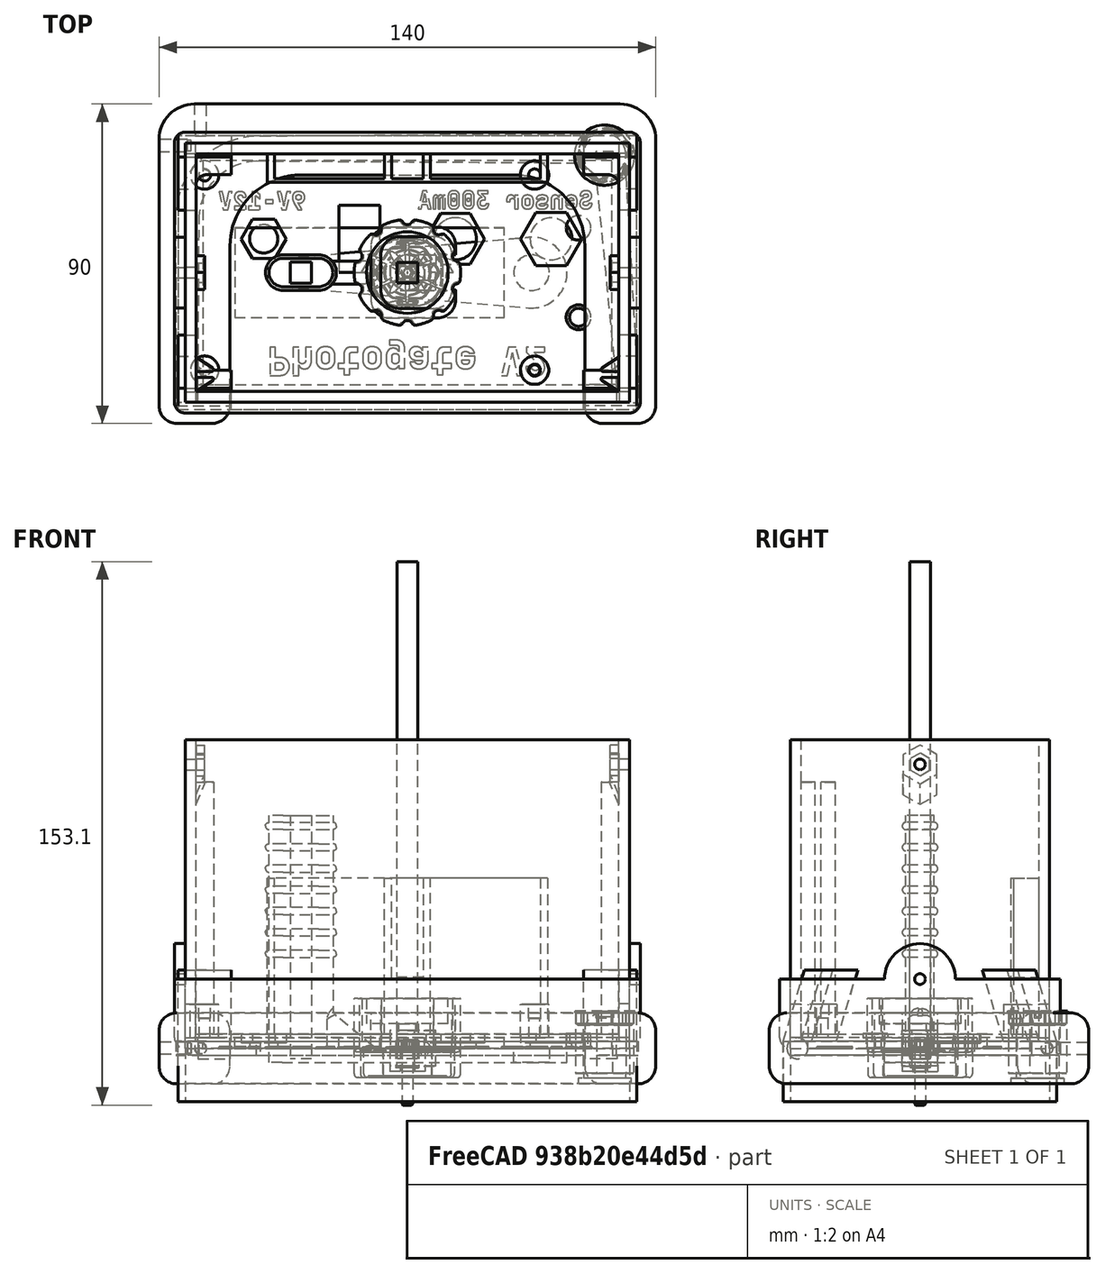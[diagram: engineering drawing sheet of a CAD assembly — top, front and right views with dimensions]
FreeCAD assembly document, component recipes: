
FREECAD ASSEMBLY — COMPONENT RECIPES ("All_Models")

This assembly document has 21 components, labeled P0..P20 below (a component is one placed body or linked part). 17 of them carry a construction recipe — the FreeCAD feature program that regenerates the part from scratch, quoted from this document or its linked companion documents; the rest are supplied as boundary geometry only. No exploded tour is included for this assembly.
NOTE — this tour is split across 2 documents so each fits a 32k-token context. This is document 1: the component sections continue in the remaining 1 document, each repeating the header above.
COMPONENT P0 — recipe-attached ("Arm001", modeled in this document).
Construction recipe (the document's own serialized feature program — sketch geometry with constraints, then the solid features built on it; lengths are millimeters unless a unit is written):

FEATURE [Sketcher::SketchObject] Sketch010
  ArcFitTolerance = 1e-06
  AttachmentSupport = -> [XY_Plane002]
  ExternalTypes = [0]
  FullyConstrained = true
  MakeInternals = false
  MapMode = 5
  _ExternalGeoVersion = 0
  sketch-geometry (9):
    g0: ArcOfCircle CenterX=-35 CenterY=0 CenterZ=0 NormalX=0 NormalY=0 NormalZ=1 AngleXU=0 Radius=4 StartAngle=1.65662 EndAngle=4.62657
    g1: ArcOfCircle CenterX=35 CenterY=0 CenterZ=0 NormalX=0 NormalY=0 NormalZ=1 AngleXU=0 Radius=10 StartAngle=4.62657 EndAngle=7.9398
    g2: LineSegment StartX=-35.3429 StartY=3.98528 StartZ=0 EndX=34.1429 EndY=9.9632 EndZ=0
    g3: LineSegment StartX=-35.3429 StartY=-3.98528 StartZ=0 EndX=34.1429 EndY=-9.9632 EndZ=0
    g4: ArcOfCircle CenterX=-35 CenterY=0 CenterZ=0 NormalX=0 NormalY=0 NormalZ=1 AngleXU=0 Radius=4 StartAngle=1.5708 EndAngle=4.71239
    g5: ArcOfCircle CenterX=-25 CenterY=-1e-16 CenterZ=0 NormalX=0 NormalY=0 NormalZ=1 AngleXU=0 Radius=4 StartAngle=4.71239 EndAngle=7.85398
    g6: LineSegment StartX=-35 StartY=4 StartZ=0 EndX=-25 EndY=4 EndZ=0
    g7: LineSegment StartX=-35 StartY=-4 StartZ=0 EndX=-25 EndY=-4 EndZ=0
    g8: Circle CenterX=35 CenterY=0 CenterZ=0 NormalX=0 NormalY=0 NormalZ=1 AngleXU=0 Radius=5
  constraints (20):
    c: Tangent(g0,g2) = 1.5708
    c: Tangent(g0,g3) = -1.5708
    c: Tangent(g1,g2) = 1.5708
    c: Tangent(g1,g3) = -1.5708
    c: Symmetric(g0,g1,g-1)
    c: DistanceX(g0,g1) = 70
    c: PointOnObject(g0,g-1)
    c: Radius(g0) = 4
    c: Radius(g1) = 10
    c: Tangent(g4,g6) = 1.5708
    c: Tangent(g4,g7) = -1.5708
    c: Tangent(g5,g6) = 1.5708
    c: Tangent(g5,g7) = -1.5708
    c: Equal(g4,g5)
    c: Horizontal(g7)
    c: Coincident(g4,g0)
    c: Tangent(g4,g0)
    c: DistanceX(g0,g5) = 10
    c: Diameter(g8) = 10
    c: Coincident(g8,g1)
FEATURE [PartDesign::Pad] Pad009
  Direction = (0,0,1)
  Length = 4
  Length2 = 10
  Profile = -> Sketch010 [Edge1,Edge2,Edge4,Edge9,Edge3]
  ReferenceAxis = -> Sketch010 [N_Axis]
  Refine = true
  Reversed = true
  SideType = 0
  Suppressed = false
  Type = 0
  Type2 = 0
FEATURE [PartDesign::Pad] Pad010
  BaseFeature = -> Pad009
  Direction = (0,0,1)
  Length = 65.65
  Length2 = 10
  Profile = -> Sketch010 [Edge7,Edge6,Vertex6,Edge5,Edge8]
  ReferenceAxis = -> Sketch010 [N_Axis]
  Refine = true
  SideType = 0
  Suppressed = false
  Type = 0
  Type2 = 0
  expr: Length = Sketch001.Constraints.display_inner_length / 2 + 3 mm
FEATURE [Sketcher::SketchObject] Sketch011
  ArcFitTolerance = 1e-06
  AttachmentOffset = pos=(0,0,-2) rot=(0,0,1;0rad)
  AttachmentSupport = -> [Pad010]
  ExternalTypes = [0]
  FullyConstrained = true
  MakeInternals = false
  MapMode = 5
  Placement = pos=(0,0,63.65) rot=(0,0,1;0rad)
  _ExternalGeoVersion = 0
  sketch-geometry (4):
    g0: ArcOfCircle CenterX=-35 CenterY=0 CenterZ=0 NormalX=0 NormalY=0 NormalZ=1 AngleXU=0 Radius=5 StartAngle=1.5708 EndAngle=4.71239
    g1: ArcOfCircle CenterX=-25 CenterY=-1e-16 CenterZ=0 NormalX=0 NormalY=0 NormalZ=1 AngleXU=0 Radius=5 StartAngle=4.71239 EndAngle=7.85398
    g2: LineSegment StartX=-35 StartY=5 StartZ=0 EndX=-25 EndY=5 EndZ=0
    g3: LineSegment StartX=-35 StartY=-5 StartZ=0 EndX=-25 EndY=-5 EndZ=0
  constraints (8):
    c: Tangent(g0,g2) = 1.5708
    c: Tangent(g0,g3) = -1.5708
    c: Tangent(g1,g2) = 1.5708
    c: Tangent(g1,g3) = -1.5708
    c: Equal(g0,g1)
    c: Radius(g1) = 5
    c: Coincident(g1,g-3)
    c: Coincident(g0,g-4)
FEATURE [PartDesign::Pad] Pad011
  BaseFeature = -> Pad010
  Direction = (0,0,1)
  Length = 2
  Length2 = 10
  Profile = -> Sketch011
  ReferenceAxis = -> Sketch011 [N_Axis]
  Refine = true
  Reversed = true
  SideType = 0
  Suppressed = false
  Type = 0
  Type2 = 0
FEATURE [PartDesign::Fillet] Fillet001
  Base = -> Pad011 [Face14]
  BaseFeature = -> Pad011
  Radius = 0.99
  Refine = true
  SupportTransform = false
  Suppressed = false
  UseAllEdges = false
FEATURE [PartDesign::LinearPattern] LinearPattern
  BaseFeature = -> Fillet001
  Direction = -> Z_Axis002
  Length = 36
  Length2 = 100
  Mode = 1
  Mode2 = 0
  Occurrences = 7
  Occurrences2 = 1
  Offset = 6
  Offset2 = 10
  Originals = -> [Pad011,Fillet001]
  Refine = true
  Reversed = true
  Reversed2 = false
  SpacingPattern = [0]
  SpacingPattern2 = [0]
  Spacings = [-1,-1,-1,-1,-1,-1]
  Suppressed = false
  TransformMode = 0
FEATURE [Sketcher::SketchObject] Sketch057
  ArcFitTolerance = 1e-06
  ExternalTypes = [0]
  FullyConstrained = true
  MakeInternals = false
  MapMode = 5
  _ExternalGeoVersion = 0
  sketch-geometry (5):
    g0: ArcOfCircle CenterX=-25 CenterY=0 CenterZ=0 NormalX=0 NormalY=0 NormalZ=1 AngleXU=0 Radius=3.99999 StartAngle=5.32325 EndAngle=7.24312
    g1: LineSegment StartX=-22.7057 StartY=-3.2766 StartZ=0 EndX=-9.00001 EndY=-3.2766 EndZ=0
    g2: LineSegment StartX=-22.7057 StartY=3.2766 StartZ=0 EndX=-9.00001 EndY=3.2766 EndZ=0
    g3: LineSegment StartX=-9.00001 StartY=3.2766 StartZ=0 EndX=-9.00001 EndY=-3.2766 EndZ=0
    g4: GeomPoint X=-21 Y=0 Z=0
  constraints (14):
    c: Coincident(g0,g-3)
    c: PointOnObject(g0,g-3)
    c: Coincident(g1,g0)
    c: Horizontal(g1)
    c: Coincident(g2,g0)
    c: Horizontal(g2)
    c: Coincident(g3,g2)
    c: Coincident(g3,g1)
    c: Vertical(g3)
    c: Angle(g0) = 1.91986
    c: Vertical(g0,g0)
    c: PointOnObject(g4,g-1)
    c: PointOnObject(g4,g0)
    c: DistanceX(g4,g2) = 12
FEATURE [PartDesign::Pad] Pad033
  BaseFeature = -> LinearPattern
  Direction = (-1.2,0,1)
  Length = 12
  Length2 = 10
  Profile = -> Sketch057
  ReferenceAxis = -> Sketch057 [N_Axis]
  Refine = true
  SideType = 0
  Suppressed = false
  Type = 0
  Type2 = 0
  UseCustomVector = true
FEATURE [PartDesign::Fillet] Fillet006
  Base = -> Pad033 [Face137]
  BaseFeature = -> Pad033
  Radius = 2.5
  Refine = true
  SupportTransform = false
  Suppressed = false
  UseAllEdges = false
FEATURE [Sketcher::SketchObject] Sketch045
  ArcFitTolerance = 1e-06
  AttachmentSupport = -> [Fillet006]
  ExternalTypes = [0]
  FullyConstrained = true
  MakeInternals = false
  MapMode = 5
  Placement = pos=(0,0,65.65) rot=(0,0,1;0rad)
  _ExternalGeoVersion = 0
  sketch-geometry (5):
    g0: LineSegment StartX=-33 StartY=-2.99999 StartZ=0 EndX=-27 EndY=-2.99999 EndZ=0
    g1: LineSegment StartX=-27 StartY=-2.99999 StartZ=0 EndX=-27 EndY=2.99999 EndZ=0
    g2: LineSegment StartX=-27 StartY=2.99999 StartZ=0 EndX=-33 EndY=2.99999 EndZ=0
    g3: LineSegment StartX=-33 StartY=2.99999 StartZ=0 EndX=-33 EndY=-2.99999 EndZ=0
    g4: GeomPoint [constr] X=-30 Y=0 Z=0
  constraints (13):
    c: Coincident(g0,g1)
    c: Coincident(g1,g2)
    c: Coincident(g2,g3)
    c: Coincident(g3,g0)
    c: Horizontal(g0)
    c: Horizontal(g2)
    c: Vertical(g1)
    c: Vertical(g3)
    c: Symmetric(g2,g0,g4)
    c: Symmetric(g-3,g-4,g4)
    c: DistanceY(g-4,g0) = 1
    c: Equal(g0,g1)
    c: DistanceY(g1,g1) = 5.99999  'reforce_arm_width'
FEATURE [PartDesign::Pocket] Pocket030
  BaseFeature = -> Fillet006
  Direction = (0,0,-1)
  Length = 5
  Length2 = 5
  Offset = -1
  Profile = -> Sketch045
  ReferenceAxis = -> Sketch045 [N_Axis]
  Refine = true
  SideType = 0
  Suppressed = false
  Type = 2
  Type2 = 0
FEATURE [PartDesign::Body] Body002  label="Arm"
  AllowCompound = false
  Group = -> [Sketch010,Pad009,Pad010,Sketch011,Pad011,Fillet001,LinearPattern,Sketch045,Sketch057,Pad033,Fillet006,Pocket030]
  Origin = -> Origin002
  Tip = -> Pocket030
COMPONENT P1 — same part as P0; its construction recipe is shown at P0.
COMPONENT P2 — recipe-attached ("Box001", modeled in this document).
Construction recipe (the document's own serialized feature program — sketch geometry with constraints, then the solid features built on it; lengths are millimeters unless a unit is written):

FEATURE [Sketcher::SketchObject] Sketch
  ArcFitTolerance = 1e-06
  AttachmentSupport = -> [XY_Plane]
  ExternalTypes = [0]
  FullyConstrained = true
  MakeInternals = false
  MapMode = 5
  _ExternalGeoVersion = 0
  expr: Constraints[22] = Sketch001.Constraints.display_inner_width - 0.1 mm
  expr: Constraints[23] = Sketch001.Constraints.display_inner_length - 0.1 mm
  sketch-geometry (10):
    g0: LineSegment StartX=-59.6 StartY=-33.5 StartZ=0 EndX=59.6 EndY=-33.5 EndZ=0
    g1: LineSegment StartX=59.6 StartY=-33.5 StartZ=0 EndX=59.6 EndY=33.5 EndZ=0
    g2: LineSegment StartX=59.6 StartY=33.5 StartZ=0 EndX=-59.6 EndY=33.5 EndZ=0
    g3: LineSegment StartX=-59.6 StartY=33.5 StartZ=0 EndX=-59.6 EndY=-33.5 EndZ=0
    g4: GeomPoint [constr] X=0 Y=0 Z=0
    g5: LineSegment StartX=-62.6 StartY=-36.5 StartZ=0 EndX=62.6 EndY=-36.5 EndZ=0
    g6: LineSegment StartX=62.6 StartY=-36.5 StartZ=0 EndX=62.6 EndY=36.5 EndZ=0
    g7: LineSegment StartX=62.6 StartY=36.5 StartZ=0 EndX=-62.6 EndY=36.5 EndZ=0
    g8: LineSegment StartX=-62.6 StartY=36.5 StartZ=0 EndX=-62.6 EndY=-36.5 EndZ=0
    g9: GeomPoint [constr] X=0 Y=0 Z=0
  constraints (24):
    c: Coincident(g0,g1)
    c: Coincident(g1,g2)
    c: Coincident(g2,g3)
    c: Coincident(g3,g0)
    c: Horizontal(g0)
    c: Horizontal(g2)
    c: Vertical(g1)
    c: Vertical(g3)
    c: Symmetric(g2,g0,g4)
    c: Coincident(g4,g-1)
    c: Coincident(g5,g6)
    c: Coincident(g6,g7)
    c: Coincident(g7,g8)
    c: Coincident(g8,g5)
    c: Horizontal(g5)
    c: Horizontal(g7)
    c: Vertical(g6)
    c: Vertical(g8)
    c: Symmetric(g7,g5,g9)
    c: Coincident(g9,g4)
    c: DistanceY(g1,g6) = 3
    c: DistanceX(g1,g6) = 3
    c: DistanceY(g8,g8) = 73
    c: DistanceX(g5,g5) = 125.2
FEATURE [PartDesign::Pad] Pad005
  Direction = (0,0,1)
  Length = 4
  Length2 = 10
  Profile = -> Sketch [Edge6,Edge5,Edge7,Edge8]
  ReferenceAxis = -> Sketch [N_Axis]
  Refine = true
  SideType = 0
  Suppressed = false
  Type = 0
  Type2 = 0
FEATURE [PartDesign::Pad] Pad006
  BaseFeature = -> Pad005
  Direction = (0,0,1)
  Length = 87
  Length2 = 10
  Profile = -> Sketch
  ReferenceAxis = -> Sketch [N_Axis]
  Refine = true
  SideType = 0
  Suppressed = false
  Type = 0
  Type2 = 0
FEATURE [Sketcher::SketchObject] Sketch007
  ArcFitTolerance = 1e-06
  AttachmentSupport = -> [Pad006]
  ExternalGeometry = -> [Pad006]
  ExternalTypes = [0]
  FullyConstrained = true
  MakeInternals = false
  MapMode = 5
  Placement = pos=(-59.6,0,0) rot=(0.57735,0.57735,0.57735;2.0944rad)
  _ExternalGeoVersion = 0
  sketch-geometry (15):
    g0: LineSegment StartX=2.75 StartY=81.5877 StartZ=0 EndX=1.24e-14 EndY=83.1754 EndZ=0
    g1: LineSegment StartX=1.24e-14 StartY=83.1754 StartZ=0 EndX=-2.75 EndY=81.5877 EndZ=0
    g2: LineSegment StartX=-2.75 StartY=81.5877 StartZ=0 EndX=-2.75 EndY=78.4123 EndZ=0
    g3: LineSegment StartX=-2.75 StartY=78.4123 StartZ=0 EndX=-2.895e-13 EndY=76.8246 EndZ=0
    g4: LineSegment StartX=-2.895e-13 StartY=76.8246 StartZ=0 EndX=2.75 EndY=78.4123 EndZ=0
    g5: LineSegment StartX=2.75 StartY=78.4123 StartZ=0 EndX=2.75 EndY=81.5877 EndZ=0
    g6: Circle [constr] CenterX=0 CenterY=80 CenterZ=0 NormalX=0 NormalY=0 NormalZ=1 AngleXU=0 Radius=3.17543
    g7: Circle CenterX=0 CenterY=80 CenterZ=0 NormalX=0 NormalY=0 NormalZ=1 AngleXU=0 Radius=1.5
    g8: LineSegment StartX=4.75 StartY=82.7424 StartZ=0 EndX=-3.91e-14 EndY=85.4848 EndZ=0
    g9: LineSegment StartX=-3.91e-14 StartY=85.4848 StartZ=0 EndX=-4.75 EndY=82.7424 EndZ=0
    g10: LineSegment StartX=-4.75 StartY=82.7424 StartZ=0 EndX=-4.75 EndY=77.2576 EndZ=0
    g11: LineSegment StartX=-4.75 StartY=77.2576 StartZ=0 EndX=3.73e-14 EndY=74.5152 EndZ=0
    g12: LineSegment StartX=3.73e-14 StartY=74.5152 StartZ=0 EndX=4.75 EndY=77.2576 EndZ=0
    g13: LineSegment StartX=4.75 StartY=77.2576 StartZ=0 EndX=4.75 EndY=82.7424 EndZ=0
    g14: Circle [constr] CenterX=0 CenterY=80 CenterZ=0 NormalX=0 NormalY=0 NormalZ=1 AngleXU=0 Radius=5.48483
  constraints (35):
    c: Coincident(g0,g1)
    c: Coincident(g1,g2)
    c: Coincident(g2,g3)
    c: Coincident(g3,g4)
    c: Coincident(g4,g5)
    c: Coincident(g5,g0)
    c: Equal(g0, g1-g5) x5
    c: PointOnObject(g0,g6)
    c: PointOnObject(g1,g6)
    c: PointOnObject(g2,g6)
    c: PointOnObject(g3,g6)
    c: PointOnObject(g4,g6)
    c: PointOnObject(g5,g6)
    c: PointOnObject(g6,g-2)
    c: Coincident(g7,g6)
    c: Diameter(g7) = 3
    c: DistanceX(g1,g0) = 5.5
    c: Horizontal(g0,g1)
    c: DistanceY(g6,g-3) = 7  'gap_box_painel'
    c: Coincident(g8,g9)
    c: Coincident(g9,g10)
    c: Coincident(g10,g11)
    c: Coincident(g11,g12)
    c: Coincident(g12,g13)
    c: Coincident(g13,g8)
    c: Equal(g8, g9-g13) x5
    c: PointOnObject(g8,g14)
    c: PointOnObject(g9,g14)
    c: PointOnObject(g10,g14)
    c: PointOnObject(g11,g14)
    c: PointOnObject(g12,g14)
    c: PointOnObject(g13,g14)
    c: Coincident(g14,g6)
    c: Vertical(g13)
    c: DistanceX(g0,g8) = 2
FEATURE [PartDesign::Pocket] Pocket005
  BaseFeature = -> Pad006
  Direction = (-1,0,0)
  Length = 5
  Length2 = 5
  Profile = -> Sketch007 [Edge7]
  ReferenceAxis = -> Sketch007 [N_Axis]
  Refine = true
  SideType = 0
  Suppressed = false
  Type = 1
  Type2 = 0
FEATURE [PartDesign::Pad] Pad007
  BaseFeature = -> Pocket005
  Direction = (1,0,0)
  Length = 2.5
  Length2 = 10
  Profile = -> Sketch007 [Edge12,Edge5,Edge4,Edge11,Edge10,Edge3,Edge2,Edge1,Edge6,Edge13,Edge8,Edge9]
  ReferenceAxis = -> Sketch007 [N_Axis]
  Refine = true
  SideType = 0
  Suppressed = false
  Type = 0
  Type2 = 0
FEATURE [PartDesign::Chamfer] Chamfer
  Angle = 45
  Base = -> Pad007 [Edge26,Edge31]
  BaseFeature = -> Pad007
  ChamferType = 1
  FlipDirection = false
  Refine = true
  Size = 5
  Size2 = 2.4999
  SupportTransform = false
  Suppressed = false
  UseAllEdges = false
FEATURE [Sketcher::SketchObject] Sketch008
  ArcFitTolerance = 1e-06
  AttachmentSupport = -> [Chamfer]
  ExternalGeometry = -> [Chamfer]
  ExternalTypes = [0]
  FullyConstrained = true
  MakeInternals = false
  MapMode = 5
  Placement = pos=(0,0,4) rot=(0,0,1;0rad)
  _ExternalGeoVersion = 0
  sketch-geometry (10):
    g0: LineSegment StartX=-59.6 StartY=-33.5 StartZ=0 EndX=-59.6 EndY=-29.5 EndZ=0
    g1: LineSegment StartX=-59.6 StartY=-29.5 StartZ=0 EndX=-55.1 EndY=-29.5 EndZ=0
    g2: LineSegment StartX=-54.8288 StartY=-30.4201 StartZ=0 EndX=-59.6 EndY=-33.5 EndZ=0
    g3: ArcOfCircle CenterX=-55.1 CenterY=-30 CenterZ=0 NormalX=0 NormalY=0 NormalZ=1 AngleXU=0 Radius=0.5 StartAngle=5.28561 EndAngle=7.85398
    g4: GeomPoint [constr] X=-53.4035 Y=-29.5 Z=0
    g5: GeomPoint X=-54.6 Y=-30 Z=0
    g6: LineSegment StartX=-59.6 StartY=-23.85 StartZ=0 EndX=-59.6 EndY=-27.85 EndZ=0
    g7: LineSegment StartX=-59.6 StartY=-27.85 StartZ=0 EndX=-55.1 EndY=-27.85 EndZ=0
    g8: LineSegment StartX=-54.8288 StartY=-26.9299 StartZ=0 EndX=-59.6 EndY=-23.85 EndZ=0
    g9: ArcOfCircle CenterX=-55.1 CenterY=-27.35 CenterZ=0 NormalX=0 NormalY=0 NormalZ=1 AngleXU=0 Radius=0.5 StartAngle=4.71239 EndAngle=7.28076
  constraints (25):
    c: Vertical(g0)
    c: Coincident(g0,g1)
    c: Horizontal(g1)
    c: DistanceY(g0,g0) = 4
    c: PointOnObject(g4,g1)
    c: PointOnObject(g4,g2)
    c: Tangent(g1,g3) = 1.5708
    c: Tangent(g2,g3) = 1.5708
    c: Radius(g3) = 0.5
    c: PointOnObject(g5,g3)
    c: DistanceX(g0,g5) = 5
    c: Horizontal(g3,g5)
    c: Vertical(g6)
    c: Coincident(g6,g7)
    c: Coincident(g8,g6)
    c: Horizontal(g7)
    c: Tangent(g7,g9) = -1.5708
    c: Tangent(g8,g9) = -1.5708
    c: Radius(g9) = 0.5
    c: Vertical(g6,g0)
    c: Vertical(g7,g1)
    c: Equal(g0,g6)
    c: DistanceY(g1,g7) = 1.65
    c: Coincident(g2,g0)
    c: Coincident(g0,g-4)
FEATURE [PartDesign::Pad] Pad008
  BaseFeature = -> Chamfer
  Direction = (0,0,1)
  Length = 10
  Length2 = 10
  Offset = 12
  Profile = -> Sketch008
  ReferenceAxis = -> Sketch008 [N_Axis]
  Refine = true
  SideType = 0
  Suppressed = false
  Type = 3
  Type2 = 0
  UpToFace = -> Chamfer [Face11]
  expr: Offset = Sketch007.Constraints.gap_box_painel + 5 mm
FEATURE [PartDesign::Mirrored] Mirrored004
  BaseFeature = -> Pad008
  MirrorPlane = -> YZ_Plane
  Originals = -> [Chamfer,Pad007,Pad008,Pocket005]
  Refine = true
  Suppressed = false
  TransformMode = 0
FEATURE [Sketcher::SketchObject] Sketch009
  ArcFitTolerance = 1e-06
  AttachmentSupport = -> [XY_Plane]
  ExternalTypes = [0]
  FullyConstrained = true
  MakeInternals = false
  MapMode = 5
  _ExternalGeoVersion = 0
  sketch-geometry (11):
    g0: Circle CenterX=40.5 CenterY=9.5 CenterZ=0 NormalX=0 NormalY=0 NormalZ=1 AngleXU=0 Radius=5.9
    g1: Circle CenterX=-40.5 CenterY=9.5 CenterZ=0 NormalX=0 NormalY=0 NormalZ=1 AngleXU=0 Radius=4
    g2: LineSegment StartX=-19.25 StartY=19 StartZ=0 EndX=-19.25 EndY=0 EndZ=0
    g3: LineSegment StartX=-19.25 StartY=0 StartZ=0 EndX=-7.75 EndY=0 EndZ=0
    g4: LineSegment StartX=-7.75 StartY=0 StartZ=0 EndX=-7.75 EndY=19 EndZ=0
    g5: LineSegment StartX=-7.75 StartY=19 StartZ=0 EndX=-19.25 EndY=19 EndZ=0
    g6: GeomPoint [constr] X=-13.5 Y=9.5 Z=0
    g7: Circle CenterX=13.5 CenterY=9.5 CenterZ=0 NormalX=0 NormalY=0 NormalZ=1 AngleXU=0 Radius=5.95
    g8: LineSegment [constr] StartX=-40.5 StartY=9.5 StartZ=0 EndX=-13.5 EndY=9.5 EndZ=0
    g9: LineSegment [constr] StartX=-13.5 StartY=9.5 StartZ=0 EndX=13.5 EndY=9.5 EndZ=0
    g10: LineSegment [constr] StartX=13.5 StartY=9.5 StartZ=0 EndX=40.5 EndY=9.5 EndZ=0
  constraints (27):
    c: Diameter(g0) = 11.8
    c: Diameter(g1) = 8
    c: Coincident(g2,g3)
    c: Coincident(g3,g4)
    c: Coincident(g4,g5)
    c: Coincident(g5,g2)
    c: Vertical(g2)
    c: Vertical(g4)
    c: Horizontal(g3)
    c: Horizontal(g5)
    c: Symmetric(g4,g2,g6)
    c: Diameter(g7) = 11.9
    c: DistanceY(g4,g4) = 19
    c: Distance(g5,g5) = 11.5
    c: Coincident(g8,g1)
    c: Horizontal(g8)
    c: Coincident(g9,g8)
    c: Coincident(g9,g7)
    c: Coincident(g10,g7)
    c: Horizontal(g10)
    c: Coincident(g10,g0)
    c: Coincident(g8,g6)
    c: Equal(g8,g9)
    c: Equal(g9,g10)
    c: Horizontal(g-1,g3)
    c: DistanceX(g8,g8) = 27
    c: Symmetric(g6,g7,g-2)
FEATURE [PartDesign::Pocket] Pocket006
  BaseFeature = -> Mirrored004
  Direction = (0,0,-1)
  Length = 5
  Length2 = 5
  Profile = -> Sketch009
  ReferenceAxis = -> Sketch009 [N_Axis]
  Refine = true
  Reversed = true
  SideType = 0
  Suppressed = false
  Type = 2
  Type2 = 0
FEATURE [Part::Part2DObjectPython] ShapeString  # Draft 2D object (typed FeaturePython)
  FontFile = <userpath>/Documents/FreeCAD/Fonts/JetBrainsMonoNerdFont-ExtraBold.ttf
  Fuse = false
  Justification = 7
  JustificationReference = 0
  KeepLeftMargin = false
  MakeFace = true
  ObliqueAngle = 0
  Placement = pos=(-41.02,17.76,1e-15) rot=(0,-1,0;3.14159rad)
  ScaleToSize = true
  Size = 5
  String = 9V-12V
  Tracking = 0
FEATURE [Part::Part2DObjectPython] ShapeString001  # Draft 2D object (typed FeaturePython)
  FontFile = <userpath>/Documents/FreeCAD/Fonts/JetBrainsMonoNerdFont-Bold.ttf
  Fuse = false
  Justification = 7
  JustificationReference = 0
  KeepLeftMargin = false
  MakeFace = true
  ObliqueAngle = 0
  Placement = pos=(13,18,1.3e-15) rot=(0,-1,0;3.14159rad)
  ScaleToSize = true
  Size = 5
  String = 300mA
  Tracking = 0
FEATURE [Part::Part2DObjectPython] ShapeString002  # Draft 2D object (typed FeaturePython)
  FontFile = <userpath>/Documents/FreeCAD/Fonts/JetBrainsMonoNerdFont-ExtraBold.ttf
  Fuse = false
  Justification = 7
  JustificationReference = 0
  KeepLeftMargin = false
  MakeFace = true
  ObliqueAngle = 0
  Placement = pos=(40,18,-4.9e-15) rot=(0,-1,0;3.14159rad)
  ScaleToSize = true
  Size = 5
  String = Sensor
  Tracking = 0
FEATURE [PartDesign::Pocket] Pocket007
  BaseFeature = -> Pocket006
  Direction = (1e-16,0,1)
  Length = 0.4
  Length2 = 5
  Profile = -> ShapeString002
  ReferenceAxis = -> ShapeString002 [N_Axis]
  Refine = true
  SideType = 0
  Suppressed = false
  Type = 0
  Type2 = 0
FEATURE [PartDesign::Pocket] Pocket008
  BaseFeature = -> Pocket007
  Direction = (1e-16,0,1)
  Length = 0.4
  Length2 = 5
  Profile = -> ShapeString001
  ReferenceAxis = -> ShapeString001 [N_Axis]
  Refine = true
  SideType = 0
  Suppressed = false
  Type = 0
  Type2 = 0
FEATURE [PartDesign::Pocket] Pocket009
  BaseFeature = -> Pocket008
  Direction = (1e-16,0,1)
  Length = 0.4
  Length2 = 5
  Profile = -> ShapeString
  ReferenceAxis = -> ShapeString [N_Axis]
  Refine = true
  SideType = 0
  Suppressed = false
  Type = 0
  Type2 = 0
FEATURE [Sketcher::SketchObject] Sketch041
  ArcFitTolerance = 1e-06
  AttachmentSupport = -> [Pocket009]
  ExternalGeometry = -> [Pocket009]
  ExternalTypes = [0]
  FullyConstrained = true
  MakeInternals = false
  MapMode = 5
  Placement = pos=(0,0,4) rot=(0,0,1;0rad)
  _ExternalGeoVersion = 0
  sketch-geometry (21):
    g0: LineSegment StartX=-34.1491 StartY=9.5 StartZ=0 EndX=-37.3246 EndY=15 EndZ=0
    g1: LineSegment StartX=-37.3246 StartY=15 StartZ=0 EndX=-43.6754 EndY=15 EndZ=0
    g2: LineSegment StartX=-43.6754 StartY=15 StartZ=0 EndX=-46.8509 EndY=9.5 EndZ=0
    g3: LineSegment StartX=-46.8509 StartY=9.5 StartZ=0 EndX=-43.6754 EndY=4 EndZ=0
    g4: LineSegment StartX=-43.6754 StartY=4 StartZ=0 EndX=-37.3246 EndY=4 EndZ=0
    g5: LineSegment StartX=-37.3246 StartY=4 StartZ=0 EndX=-34.1491 EndY=9.5 EndZ=0
    g6: Circle [constr] CenterX=-40.5 CenterY=9.5 CenterZ=0 NormalX=0 NormalY=0 NormalZ=1 AngleXU=0 Radius=6.35085
    g7: LineSegment StartX=21.7561 StartY=9.5 StartZ=0 EndX=17.6281 EndY=16.65 EndZ=0
    g8: LineSegment StartX=17.6281 StartY=16.65 StartZ=0 EndX=9.37195 EndY=16.65 EndZ=0
    g9: LineSegment StartX=9.37195 StartY=16.65 StartZ=0 EndX=5.24389 EndY=9.5 EndZ=0
    g10: LineSegment StartX=5.24389 StartY=9.5 StartZ=0 EndX=9.37195 EndY=2.35 EndZ=0
    g11: LineSegment StartX=9.37195 StartY=2.35 StartZ=0 EndX=17.6281 EndY=2.35 EndZ=0
    g12: LineSegment StartX=17.6281 StartY=2.35 StartZ=0 EndX=21.7561 EndY=9.5 EndZ=0
    g13: Circle [constr] CenterX=13.5 CenterY=9.5 CenterZ=0 NormalX=0 NormalY=0 NormalZ=1 AngleXU=0 Radius=8.25611
    g14: LineSegment StartX=49.1603 StartY=9.5 StartZ=0 EndX=44.8301 EndY=17 EndZ=0
    g15: LineSegment StartX=44.8301 StartY=17 StartZ=0 EndX=36.1699 EndY=17 EndZ=0
    g16: LineSegment StartX=36.1699 StartY=17 StartZ=0 EndX=31.8397 EndY=9.5 EndZ=0
    g17: LineSegment StartX=31.8397 StartY=9.5 StartZ=0 EndX=36.1699 EndY=2 EndZ=0
    g18: LineSegment StartX=36.1699 StartY=2 StartZ=0 EndX=44.8301 EndY=2 EndZ=0
    g19: LineSegment StartX=44.8301 StartY=2 StartZ=0 EndX=49.1603 EndY=9.5 EndZ=0
    g20: Circle [constr] CenterX=40.5 CenterY=9.5 CenterZ=0 NormalX=0 NormalY=0 NormalZ=1 AngleXU=0 Radius=8.66025
  constraints (48):
    c: Coincident(g0,g1)
    c: Coincident(g1,g2)
    c: Coincident(g2,g3)
    c: Coincident(g3,g4)
    c: Coincident(g4,g5)
    c: Coincident(g5,g0)
    c: Equal(g0, g1-g5) x5
    c: PointOnObject(g0,g6)
    c: PointOnObject(g1,g6)
    c: PointOnObject(g2,g6)
    c: PointOnObject(g3,g6)
    c: PointOnObject(g4,g6)
    c: PointOnObject(g5,g6)
    c: Coincident(g6,g-3)
    c: Coincident(g7,g8)
    c: Coincident(g8,g9)
    c: Coincident(g9,g10)
    c: Coincident(g10,g11)
    c: Coincident(g11,g12)
    c: Coincident(g12,g7)
    c: Equal(g7, g8-g12) x5
    c: PointOnObject(g7,g13)
    c: PointOnObject(g8,g13)
    c: PointOnObject(g9,g13)
    c: PointOnObject(g10,g13)
    c: PointOnObject(g11,g13)
    c: PointOnObject(g12,g13)
    c: Coincident(g13,g-4)
    c: Coincident(g14,g15)
    c: Coincident(g15,g16)
    c: Coincident(g16,g17)
    c: Coincident(g17,g18)
    c: Coincident(g18,g19)
    c: Coincident(g19,g14)
    c: Equal(g14, g15-g19) x5
    c: PointOnObject(g14,g20)
    c: PointOnObject(g15,g20)
    c: PointOnObject(g16,g20)
    c: PointOnObject(g17,g20)
    c: PointOnObject(g18,g20)
    c: PointOnObject(g19,g20)
    c: Coincident(g20,g-5)
    c: Horizontal(g4)
    c: Horizontal(g11)
    c: Horizontal(g18)
    c: DistanceY(g4,g0) = 11
    c: DistanceY(g11,g7) = 14.3
    c: DistanceY(g18,g14) = 15
FEATURE [PartDesign::Pocket] Pocket023
  BaseFeature = -> Pocket009
  Direction = (0,0,-1)
  Length = 2.5
  Length2 = 5
  Profile = -> Sketch041
  ReferenceAxis = -> Sketch041 [N_Axis]
  Refine = true
  SideType = 0
  Suppressed = false
  Type = 0
  Type2 = 0
FEATURE [Sketcher::SketchObject] Sketch042
  ArcFitTolerance = 1e-06
  AttachmentOffset = pos=(0,0,7) rot=(0,0,1;0rad)
  AttachmentSupport = -> [Pocket023]
  ExternalGeometry = -> [Pocket023]
  ExternalTypes = [0]
  FullyConstrained = true
  MakeInternals = false
  MapMode = 5
  Placement = pos=(0,26.5,1.6e-15) rot=(1,0,0;1.5708rad)
  _ExternalGeoVersion = 0
  sketch-geometry (18):
    g0: LineSegment StartX=-37.5 StartY=48 StartZ=0 EndX=-37.5 EndY=4 EndZ=0
    g1: LineSegment [constr] StartX=-37.5 StartY=4 StartZ=0 EndX=-6.5 EndY=4 EndZ=0
    g2: LineSegment StartX=6.5 StartY=48 StartZ=0 EndX=6.5 EndY=4 EndZ=0
    g3: LineSegment [constr] StartX=6.5 StartY=4 StartZ=0 EndX=37.5 EndY=4 EndZ=0
    g4: LineSegment StartX=37.5 StartY=4 StartZ=0 EndX=37.5 EndY=48 EndZ=0
    g5: LineSegment StartX=-39.5 StartY=48 StartZ=0 EndX=-39.5 EndY=4 EndZ=0
    g6: LineSegment StartX=-6.5 StartY=48 StartZ=0 EndX=-6.5 EndY=4 EndZ=0
    g7: LineSegment StartX=39.5 StartY=4 StartZ=0 EndX=39.5 EndY=48 EndZ=0
    g8: LineSegment StartX=4.5 StartY=20 StartZ=0 EndX=4.5 EndY=48 EndZ=0
    g9: LineSegment StartX=-37.5 StartY=48 StartZ=0 EndX=-39.5 EndY=48 EndZ=0
    g10: LineSegment StartX=-4.5 StartY=48 StartZ=0 EndX=-6.5 EndY=48 EndZ=0
    g11: LineSegment StartX=4.5 StartY=48 StartZ=0 EndX=6.5 EndY=48 EndZ=0
    g12: LineSegment StartX=37.5 StartY=48 StartZ=0 EndX=39.5 EndY=48 EndZ=0
    g13: LineSegment StartX=-4.5 StartY=48 StartZ=0 EndX=-4.5 EndY=20 EndZ=0
    g14: LineSegment StartX=-4.5 StartY=20 StartZ=0 EndX=4.5 EndY=20 EndZ=0
    g15: LineSegment StartX=-39.5 StartY=4 StartZ=0 EndX=-37.5 EndY=4 EndZ=0
    g16: LineSegment StartX=-6.5 StartY=4 StartZ=0 EndX=6.5 EndY=4 EndZ=0
    g17: LineSegment StartX=37.5 StartY=4 StartZ=0 EndX=39.5 EndY=4 EndZ=0
  constraints (51):
    c: Coincident(g0,g1)
    c: Vertical(g0)
    c: Coincident(g2,g3)
    c: Coincident(g3,g4)
    c: Vertical(g4)
    c: Horizontal(g3)
    c: Vertical(g5)
    c: Vertical(g6)
    c: Vertical(g7)
    c: DistanceX(g4,g7) = 2
    c: Coincident(g1,g6)
    c: Vertical(g8)
    c: Horizontal(g-3,g5)
    c: Vertical(g2)
    c: Coincident(g9,g0)
    c: Horizontal(g9)
    c: Coincident(g5,g9)
    c: Coincident(g11,g8)
    c: Coincident(g11,g2)
    c: Horizontal(g11)
    c: Coincident(g12,g4)
    c: Coincident(g12,g7)
    c: Horizontal(g12)
    c: Horizontal(g2,g4)
    c: Equal(g12,g11)
    c: Equal(g10,g11)
    c: Equal(g10,g9)
    c: DistanceY(g0,g0) = 44
    c: Horizontal(g1)
    c: Coincident(g6,g10)
    c: Horizontal(g10)
    c: Horizontal(g0,g6)
    c: Equal(g1,g3)
    c: DistanceX(g1,g1) = 31
    c: Symmetric(g10,g8,g-2)
    c: Coincident(g13,g10)
    c: Vertical(g13)
    c: Horizontal(g1,g2)
    c: DistanceY(g8,g8) = 28
    c: Horizontal(g13,g8)
    c: Coincident(g14,g13)
    c: Coincident(g14,g8)
    c: Coincident(g15,g5)
    c: Coincident(g15,g0)
    c: Coincident(g16,g1)
    c: Coincident(g16,g2)
    c: Coincident(g17,g3)
    c: Coincident(g17,g7)
    c: Horizontal(g17)
    c: Horizontal(g15)
    c: DistanceX(g14,g14) = 9
FEATURE [PartDesign::Pad] Pad018
  BaseFeature = -> Pocket023
  Direction = (0,-1,2e-16)
  Length = 10
  Length2 = 10
  Profile = -> Sketch042
  ReferenceAxis = -> Sketch042 [N_Axis]
  Refine = true
  Reversed = true
  SideType = 0
  Suppressed = false
  Type = 2
  Type2 = 0
FEATURE [Sketcher::SketchObject] Sketch043
  ArcFitTolerance = 1e-06
  AttachmentSupport = -> [Pad018]
  ExternalGeometry = -> [Pad018]
  ExternalTypes = [0]
  FullyConstrained = true
  MakeInternals = false
  MapMode = 5
  Placement = pos=(0,26.5,-6.4e-15) rot=(1,0,0;1.5708rad)
  _ExternalGeoVersion = 0
  sketch-geometry (4):
    g0: LineSegment StartX=-39.5 StartY=48 StartZ=0 EndX=-39.5 EndY=4 EndZ=0
    g1: LineSegment StartX=-39.5 StartY=4 StartZ=0 EndX=39.5 EndY=4 EndZ=0
    g2: LineSegment StartX=39.5 StartY=4 StartZ=0 EndX=39.5 EndY=48 EndZ=0
    g3: LineSegment StartX=39.5 StartY=48 StartZ=0 EndX=-39.5 EndY=48 EndZ=0
  constraints (10):
    c: Coincident(g0,g1)
    c: Coincident(g1,g2)
    c: Coincident(g2,g3)
    c: Coincident(g3,g0)
    c: Vertical(g0)
    c: Vertical(g2)
    c: Horizontal(g1)
    c: Horizontal(g3)
    c: Coincident(g0,g-3)
    c: Coincident(g1,g-4)
FEATURE [PartDesign::Pad] Pad019
  BaseFeature = -> Pad018
  Direction = (0,-1,2e-16)
  Length = 1
  Length2 = 10
  Profile = -> Sketch043
  ReferenceAxis = -> Sketch043 [N_Axis]
  Refine = true
  SideType = 0
  Suppressed = false
  Type = 0
  Type2 = 0
FEATURE [PartDesign::Body] Body  label="Box"
  AllowCompound = false
  Group = -> [Sketch,Pad005,Pad006,Sketch007,Pocket005,Pad007,Chamfer,Sketch008,Pad008,Mirrored004,Sketch009,Pocket006,ShapeString,ShapeString001,ShapeString002,Pocket007,Pocket008,Pocket009,Sketch041,Pocket023,Sketch042,Pad018,Sketch043,Pad019]
  Origin = -> Origin
  Tip = -> Pad019
COMPONENT P3 — recipe-attached ("IrCap001", modeled in this document).
Construction recipe (the document's own serialized feature program — sketch geometry with constraints, then the solid features built on it; lengths are millimeters unless a unit is written):

FEATURE [PartDesign::SubShapeBinder] Binder
  BindCopyOnChange = 0
  BindMode = 0
  ClaimChildren = false
  Context = -> Body006 [Binder.]
  Fuse = false
  MakeFace = true
  OffsetFill = false
  OffsetIntersection = false
  OffsetJoinType = 0
  OffsetOpenResult = false
  PartialLoad = false
  Refine = true
  Relative = true
  Support = -> [Body004[Fillet004.Face12]]
  _Version = 2
FEATURE [Sketcher::SketchObject] Sketch044
  ArcFitTolerance = 1e-06
  AttachmentSupport = -> [Binder]
  ExternalGeometry = -> [Binder]
  ExternalTypes = [0]
  FullyConstrained = true
  MakeInternals = false
  MapMode = 5
  Placement = pos=(0,0,10) rot=(0,0,1;0rad)
  _ExternalGeoVersion = 0
  sketch-geometry (26):
    g0: ArcOfCircle CenterX=54.1066 CenterY=33.1066 CenterZ=0 NormalX=0 NormalY=0 NormalZ=1 AngleXU=0 Radius=0.4 StartAngle=1.5708 EndAngle=4.71239
    g1: ArcOfCircle CenterX=57.1066 CenterY=33.1066 CenterZ=0 NormalX=0 NormalY=0 NormalZ=1 AngleXU=0 Radius=0.4 StartAngle=4.71239 EndAngle=7.85398
    g2: LineSegment StartX=54.1066 StartY=33.5066 StartZ=0 EndX=57.1066 EndY=33.5066 EndZ=0
    g3: LineSegment StartX=54.1066 StartY=32.7066 StartZ=0 EndX=57.1066 EndY=32.7066 EndZ=0
    g4: LineSegment StartX=53.1066 StartY=32.1066 StartZ=0 EndX=58.1066 EndY=32.1066 EndZ=0
    g5: LineSegment StartX=58.1066 StartY=32.1066 StartZ=0 EndX=58.1066 EndY=34.1066 EndZ=0
    g6: LineSegment StartX=58.1066 StartY=34.1066 StartZ=0 EndX=53.1066 EndY=34.1066 EndZ=0
    g7: LineSegment StartX=53.1066 StartY=34.1066 StartZ=0 EndX=53.1066 EndY=32.1066 EndZ=0
    g8: GeomPoint [constr] X=55.6066 Y=33.1066 Z=0
    g9: Circle CenterX=55.6066 CenterY=33.1066 CenterZ=0 NormalX=0 NormalY=0 NormalZ=1 AngleXU=0 Radius=8.5
    g10: LineSegment StartX=57.7677 StartY=41.1721 StartZ=0 EndX=49.7023 EndY=39.0109 EndZ=0
    g11: LineSegment StartX=49.7023 StartY=39.0109 StartZ=0 EndX=47.5411 EndY=30.9455 EndZ=0
    g12: LineSegment StartX=47.5411 StartY=30.9455 StartZ=0 EndX=53.4455 EndY=25.0411 EndZ=0
    g13: LineSegment StartX=53.4455 StartY=25.0411 StartZ=0 EndX=61.5109 EndY=27.2023 EndZ=0
    g14: LineSegment StartX=61.5109 StartY=27.2023 StartZ=0 EndX=63.6721 EndY=35.2677 EndZ=0
    g15: LineSegment StartX=63.6721 StartY=35.2677 StartZ=0 EndX=57.7677 EndY=41.1721 EndZ=0
    g16: Circle [constr] CenterX=55.6066 CenterY=33.1066 CenterZ=0 NormalX=0 NormalY=0 NormalZ=1 AngleXU=0 Radius=8.35
    g17: LineSegment StartX=57.4183 StartY=39.8681 StartZ=0 EndX=50.6569 EndY=38.0563 EndZ=0
    g18: LineSegment StartX=50.6569 StartY=38.0563 StartZ=0 EndX=48.8451 EndY=31.2949 EndZ=0
    g19: LineSegment StartX=48.8451 StartY=31.2949 StartZ=0 EndX=53.7949 EndY=26.3451 EndZ=0
    g20: LineSegment StartX=53.7949 StartY=26.3451 StartZ=0 EndX=60.5563 EndY=28.1569 EndZ=0
    g21: LineSegment StartX=60.5563 StartY=28.1569 StartZ=0 EndX=62.3681 EndY=34.9183 EndZ=0
    g22: LineSegment StartX=62.3681 StartY=34.9183 StartZ=0 EndX=57.4183 EndY=39.8681 EndZ=0
    g23: Circle [constr] CenterX=55.6066 CenterY=33.1066 CenterZ=0 NormalX=0 NormalY=0 NormalZ=1 AngleXU=0 Radius=7
    g24: LineSegment [constr] StartX=57.8066 StartY=41.317 StartZ=0 EndX=57.7677 EndY=41.1721 EndZ=0
    g25: LineSegment [constr] StartX=57.7677 StartY=41.1721 StartZ=0 EndX=57.4183 EndY=39.8681 EndZ=0
  constraints (60):
    c: Tangent(g0,g2) = 1.5708
    c: Tangent(g0,g3) = -1.5708
    c: Tangent(g1,g2) = 1.5708
    c: Tangent(g1,g3) = -1.5708
    c: Equal(g0,g1)
    c: Horizontal(g2)
    c: Radius(g0) = 0.4
    c: DistanceX(g2,g2) = 3
    c: Coincident(g4,g5)
    c: Coincident(g5,g6)
    c: Coincident(g6,g7)
    c: Coincident(g7,g4)
    c: Horizontal(g4)
    c: Horizontal(g6)
    c: Vertical(g5)
    c: Vertical(g7)
    c: Symmetric(g6,g4,g8)
    c: DistanceX(g6,g6) = 5
    c: DistanceY(g5,g5) = 2
    c: PointOnObject(g-4,g9)
    c: PointOnObject(g-5,g9)
    c: PointOnObject(g-3,g9)
    c: Coincident(g8,g9)
    c: Symmetric(g0,g1,g8)
    c: Coincident(g10,g11)
    c: Coincident(g11,g12)
    c: Coincident(g12,g13)
    c: Coincident(g13,g14)
    c: Coincident(g14,g15)
    c: Coincident(g15,g10)
    c: Equal(g10, g11-g15) x5
    c: PointOnObject(g10,g16)
    c: PointOnObject(g11,g16)
    c: PointOnObject(g12,g16)
    c: PointOnObject(g13,g16)
    c: PointOnObject(g14,g16)
    c: PointOnObject(g15,g16)
    c: Coincident(g16,g8)
    c: Coincident(g17,g18)
    c: Coincident(g18,g19)
    c: Coincident(g19,g20)
    c: Coincident(g20,g21)
    c: Coincident(g21,g22)
    c: Coincident(g22,g17)
    c: Equal(g17, g18-g22) x5
    c: PointOnObject(g17,g23)
    c: PointOnObject(g18,g23)
    c: PointOnObject(g19,g23)
    c: PointOnObject(g20,g23)
    c: PointOnObject(g21,g23)
    c: PointOnObject(g22,g23)
    c: Coincident(g23,g8)
    c: Diameter(g16) = 16.7
    c: Diameter(g23) = 14
    c: Coincident(g24,g-3)
    c: Coincident(g24,g10)
    c: Coincident(g25,g10)
    c: Coincident(g25,g17)
    c: Parallel(g25,g24)
    c: Perpendicular(g9,g24)
FEATURE [PartDesign::Pad] Pad020
  Direction = (0,0,1)
  Length = 0.5
  Length2 = 10
  Profile = -> Sketch044 [Edge9,Edge2,Edge3,Edge4,Edge1]
  ReferenceAxis = -> Sketch044 [N_Axis]
  Refine = true
  SideType = 0
  Suppressed = false
  Type = 0
  Type2 = 0
FEATURE [PartDesign::Pad] Pad025
  BaseFeature = -> Pad020
  Direction = (0,0,1)
  Length = 1
  Length2 = 10
  Profile = -> Sketch044 [Edge6,Edge3,Edge4,Edge7,Edge2,Edge5,Edge8,Edge1]
  ReferenceAxis = -> Sketch044 [N_Axis]
  Refine = true
  Reversed = true
  SideType = 0
  Suppressed = false
  Type = 0
  Type2 = 0
FEATURE [PartDesign::SubShapeBinder] Binder001
  BindCopyOnChange = 0
  BindMode = 0
  ClaimChildren = false
  Context = -> Body006 [Binder001.]
  Fuse = false
  MakeFace = true
  OffsetFill = false
  OffsetIntersection = false
  OffsetJoinType = 0
  OffsetOpenResult = false
  PartialLoad = false
  Refine = true
  Relative = true
  Support = -> [Pad025[Edge18,Edge16,Edge14,Edge19]]
  _Version = 2
FEATURE [PartDesign::Pad] Pad026
  BaseFeature = -> Pad025
  Direction = (0,0,1)
  Length = 0.4
  Length2 = 10
  Profile = -> Pad025 [Edge18,Edge16,Edge14,Edge19]
  Refine = true
  Reversed = true
  SideType = 0
  Suppressed = false
  Type = 0
  Type2 = 0
FEATURE [PartDesign::Pad] Pad027
  BaseFeature = -> Pad026
  Direction = (0,0,1)
  Length = 3.5
  Length2 = 10
  Profile = -> Sketch044 [Edge12,Edge18,Edge11,Edge17,Edge10,Edge16,Edge15,Edge21,Edge14,Edge20,Edge13,Edge19]
  ReferenceAxis = -> Sketch044 [N_Axis]
  Refine = true
  Reversed = true
  SideType = 0
  Suppressed = false
  Type = 0
  Type2 = 0
FEATURE [PartDesign::Chamfer] Chamfer001
  Angle = 45
  Base = -> Pad027 [Face13]
  BaseFeature = -> Pad027
  ChamferType = 0
  FlipDirection = false
  Refine = true
  Size = 0.4
  Size2 = 1
  SupportTransform = false
  Suppressed = false
  UseAllEdges = false
FEATURE [PartDesign::Body] Body006  label="IrCap"
  AllowCompound = false
  Group = -> [Binder,Sketch044,Pad020,Pad025,Binder001,Pad026,Pad027,Chamfer001]
  Origin = -> Origin007
  Tip = -> Chamfer001
COMPONENT P4 — recipe-attached ("IrSensor001", modeled in this document).
Construction recipe (the document's own serialized feature program — sketch geometry with constraints, then the solid features built on it; lengths are millimeters unless a unit is written):

FEATURE [Sketcher::SketchObject] Sketch016
  ArcFitTolerance = 1e-06
  AttachmentSupport = -> [XY_Plane005]
  ExternalTypes = [0]
  FullyConstrained = true
  MakeInternals = false
  MapMode = 5
  _ExternalGeoVersion = 0
  sketch-geometry (22):
    g0: LineSegment StartX=-70 StartY=-37.5 StartZ=0 EndX=-70 EndY=37.5 EndZ=0
    g1: LineSegment StartX=-60 StartY=47.5 StartZ=0 EndX=60 EndY=47.5 EndZ=0
    g2: LineSegment StartX=70 StartY=37.5 StartZ=0 EndX=70 EndY=-37.5 EndZ=0
    g3: LineSegment StartX=65 StartY=-42.5 StartZ=0 EndX=55 EndY=-42.5 EndZ=0
    g4: LineSegment StartX=50 StartY=-37.5 StartZ=0 EndX=50 EndY=7.5 EndZ=0
    g5: LineSegment StartX=30 StartY=27.5 StartZ=0 EndX=-30 EndY=27.5 EndZ=0
    g6: LineSegment StartX=-50 StartY=7.5 StartZ=0 EndX=-50 EndY=-37.5 EndZ=0
    g7: LineSegment StartX=-55 StartY=-42.5 StartZ=0 EndX=-65 EndY=-42.5 EndZ=0
    g8: ArcOfCircle CenterX=-65 CenterY=-37.5 CenterZ=0 NormalX=0 NormalY=0 NormalZ=1 AngleXU=0 Radius=5 StartAngle=3.14159 EndAngle=4.71239
    g9: ArcOfCircle CenterX=-55 CenterY=-37.5 CenterZ=0 NormalX=0 NormalY=0 NormalZ=1 AngleXU=0 Radius=5 StartAngle=4.71239 EndAngle=6.28319
    g10: ArcOfCircle CenterX=-30 CenterY=7.5 CenterZ=0 NormalX=0 NormalY=0 NormalZ=1 AngleXU=0 Radius=20 StartAngle=1.5708 EndAngle=3.14159
    g11: ArcOfCircle CenterX=30 CenterY=7.5 CenterZ=0 NormalX=0 NormalY=0 NormalZ=1 AngleXU=0 Radius=20 StartAngle=0 EndAngle=1.5708
    g12: ArcOfCircle CenterX=60 CenterY=37.5 CenterZ=0 NormalX=0 NormalY=0 NormalZ=1 AngleXU=0 Radius=10 StartAngle=0 EndAngle=1.5708
    g13: ArcOfCircle CenterX=65 CenterY=-37.5 CenterZ=0 NormalX=0 NormalY=0 NormalZ=1 AngleXU=0 Radius=5 StartAngle=4.71239 EndAngle=6.28319
    g14: ArcOfCircle CenterX=55 CenterY=-37.5 CenterZ=0 NormalX=0 NormalY=0 NormalZ=1 AngleXU=0 Radius=5 StartAngle=3.14159 EndAngle=4.71239
    g15: ArcOfCircle CenterX=-60 CenterY=37.5 CenterZ=0 NormalX=0 NormalY=0 NormalZ=1 AngleXU=0 Radius=10 StartAngle=1.5708 EndAngle=3.14159
    g16: LineSegment [constr] StartX=-30 StartY=27.5 StartZ=0 EndX=-30 EndY=47.5 EndZ=0
    g17: LineSegment [constr] StartX=-50 StartY=7.5 StartZ=0 EndX=-70 EndY=7.5 EndZ=0
    g18: Circle CenterX=55.6066 CenterY=33.1066 CenterZ=0 NormalX=0 NormalY=0 NormalZ=1 AngleXU=0 Radius=6
    g19: GeomPoint X=44.1421 Y=21.6421 Z=0
    g20: GeomPoint X=67.0711 Y=44.5711 Z=0
    g21: LineSegment [constr] StartX=44.1421 StartY=21.6421 StartZ=0 EndX=67.0711 EndY=44.5711 EndZ=0
  constraints (51):
    c: Vertical(g0)
    c: Horizontal(g1)
    c: Horizontal(g3)
    c: Vertical(g4)
    c: Horizontal(g5)
    c: Vertical(g6)
    c: Horizontal(g7)
    c: Tangent(g7,g8) = 1.5708
    c: Tangent(g0,g8) = 1.5708
    c: Tangent(g6,g9) = 1.5708
    c: Tangent(g7,g9) = 1.5708
    c: Tangent(g5,g10) = -1.5708
    c: Tangent(g6,g10) = -1.5708
    c: Tangent(g4,g11) = -1.5708
    c: Tangent(g5,g11) = -1.5708
    c: Tangent(g2,g12) = 1.5708
    c: Tangent(g1,g12) = 1.5708
    c: Tangent(g3,g13) = 1.5708
    c: Tangent(g2,g13) = 1.5708
    c: Tangent(g3,g14) = 1.5708
    c: Tangent(g4,g14) = 1.5708
    c: Tangent(g0,g15) = 1.5708
    c: Tangent(g1,g15) = 1.5708
    c: Radius(g15) = 10
    c: Radius(g10) = 20
    c: Radius(g8) = 5
    c: Equal(g15,g12)
    c: Symmetric(g6,g4,g-2)
    c: Coincident(g16,g5)
    c: PointOnObject(g16,g1)
    c: Coincident(g17,g6)
    c: PointOnObject(g17,g0)
    c: Horizontal(g17)
    c: Vertical(g16)
    c: Equal(g17,g16)
    c: DistanceY(g16,g16) = 20
    c: Symmetric(g0,g2,g-2)
    c: Equal(g8,g9)
    c: DistanceX(g6,g4) = 100
    c: DistanceY(g7,g5) = 70
    c: Symmetric(g2,g2,g-1)
    c: Equal(g14,g9)
    c: Equal(g13,g14)
    c: Diameter(g18) = 12
    c: PointOnObject(g19,g11)
    c: PointOnObject(g20,g12)
    c: Symmetric(g19,g20,g18)
    c: Coincident(g21,g19)
    c: Coincident(g21,g20)
    c: Perpendicular(g11,g21)
    c: Perpendicular(g12,g21)
FEATURE [PartDesign::Pad] Pad014
  Direction = (0,0,1)
  Length = 20
  Length2 = 10
  Profile = -> Sketch016
  ReferenceAxis = -> Sketch016 [N_Axis]
  Refine = true
  SideType = 2
  Suppressed = false
  Type = 0
  Type2 = 0
FEATURE [Sketcher::SketchObject] Sketch017
  ArcFitTolerance = 1e-06
  AttachmentSupport = -> [Pad014]
  ExternalGeometry = -> [Pad014]
  ExternalTypes = [0]
  FullyConstrained = true
  MakeInternals = false
  MapMode = 5
  Placement = pos=(-50,0,0) rot=(0.57735,0.57735,0.57735;2.0944rad)
  _ExternalGeoVersion = 0
  sketch-geometry (5):
    g0: Circle CenterX=-34.55 CenterY=0 CenterZ=0 NormalX=0 NormalY=0 NormalZ=1 AngleXU=0 Radius=2.95
    g1: ArcOfCircle CenterX=-34.55 CenterY=0 CenterZ=0 NormalX=0 NormalY=0 NormalZ=1 AngleXU=0 Radius=2.95 StartAngle=5.53819 EndAngle=7.02818
    g2: ArcOfCircle CenterX=-34.55 CenterY=0 CenterZ=0 NormalX=0 NormalY=0 NormalZ=1 AngleXU=0 Radius=2.95 StartAngle=2.3966 EndAngle=3.88658
    g3: LineSegment StartX=-32.3815 StartY=2 StartZ=0 EndX=-36.7185 EndY=2 EndZ=0
    g4: LineSegment StartX=-36.7185 StartY=-2 StartZ=0 EndX=-32.3815 EndY=-2 EndZ=0
  constraints (15):
    c: PointOnObject(g0,g-1)
    c: Tangent(g0,g-3)
    c: Diameter(g0) = 5.9  'led_diammeter'
    c: Coincident(g1,g0)
    c: PointOnObject(g1,g0)
    c: Coincident(g2,g0)
    c: PointOnObject(g2,g0)
    c: Coincident(g3,g2)
    c: Coincident(g4,g2)
    c: Coincident(g4,g1)
    c: Equal(g3,g4)
    c: Distance(g4,g3) = 4
    c: Coincident(g1,g3)
    c: Parallel(g4,g3)
    c: Horizontal(g4)
FEATURE [PartDesign::Pocket] Pocket015
  BaseFeature = -> Pad014
  Direction = (-1,0,0)
  Length = 5
  Length2 = 5
  Offset = -5
  Profile = -> Sketch017 [Edge2,Edge4,Edge3,Edge5]
  ReferenceAxis = -> Sketch017 [N_Axis]
  Refine = true
  SideType = 0
  Suppressed = false
  Type = 2
  Type2 = 0
FEATURE [PartDesign::Pocket] Pocket016
  BaseFeature = -> Pocket015
  Direction = (-1,0,0)
  Length = 9
  Length2 = 5
  Profile = -> Sketch017 [Edge1]
  ReferenceAxis = -> Sketch017 [N_Axis]
  Refine = true
  SideType = 0
  Suppressed = false
  Type = 0
  Type2 = 0
FEATURE [PartDesign::Mirrored] Mirrored006
  BaseFeature = -> Pocket016
  MirrorPlane = -> YZ_Plane005
  Originals = -> [Pocket016,Pocket015]
  Refine = true
  Suppressed = false
  TransformMode = 0
FEATURE [Sketcher::SketchObject] Sketch019
  ArcFitTolerance = 1e-06
  AttachmentSupport = -> [Mirrored006]
  ExternalGeometry = -> [Mirrored006]
  ExternalTypes = [0]
  FullyConstrained = true
  MakeInternals = false
  MapMode = 5
  Placement = pos=(0,0,10) rot=(0,0,1;0rad)
  _ExternalGeoVersion = 0
  sketch-geometry (8):
    g0: LineSegment StartX=63.817 StartY=35.3066 StartZ=0 EndX=57.8066 EndY=41.317 EndZ=0
    g1: LineSegment StartX=57.8066 StartY=41.317 StartZ=0 EndX=49.5962 EndY=39.117 EndZ=0
    g2: LineSegment StartX=49.5962 StartY=39.117 StartZ=0 EndX=47.3962 EndY=30.9066 EndZ=0
    g3: LineSegment StartX=47.3962 StartY=30.9066 StartZ=0 EndX=53.4066 EndY=24.8962 EndZ=0
    g4: LineSegment StartX=53.4066 StartY=24.8962 StartZ=0 EndX=61.617 EndY=27.0962 EndZ=0
    g5: LineSegment StartX=61.617 StartY=27.0962 StartZ=0 EndX=63.817 EndY=35.3066 EndZ=0
    g6: Circle [constr] CenterX=55.6066 CenterY=33.1066 CenterZ=0 NormalX=0 NormalY=0 NormalZ=1 AngleXU=0 Radius=8.5
    g7: LineSegment [constr] StartX=44.1421 StartY=21.6421 StartZ=0 EndX=67.0711 EndY=44.5711 EndZ=0
  constraints (20):
    c: Coincident(g0,g1)
    c: Coincident(g1,g2)
    c: Coincident(g2,g3)
    c: Coincident(g3,g4)
    c: Coincident(g4,g5)
    c: Coincident(g5,g0)
    c: Equal(g0, g1-g5) x5
    c: PointOnObject(g0,g6)
    c: PointOnObject(g1,g6)
    c: PointOnObject(g2,g6)
    c: PointOnObject(g3,g6)
    c: PointOnObject(g4,g6)
    c: PointOnObject(g5,g6)
    c: Coincident(g6,g-3)
    c: PointOnObject(g7,g-4)
    c: PointOnObject(g7,g-5)
    c: PointOnObject(g6,g7)
    c: Perpendicular(g-4,g7)
    c: Perpendicular(g3,g7)
    c: Diameter(g6) = 17
FEATURE [PartDesign::Pocket] Pocket017
  BaseFeature = -> Mirrored006
  Direction = (0,0,-1)
  Length = 17
  Length2 = 5
  Offset = 3
  Profile = -> Sketch019
  ReferenceAxis = -> Sketch019 [N_Axis]
  Refine = true
  SideType = 0
  Suppressed = false
  Type = 0
  Type2 = 0
FEATURE [Sketcher::SketchObject] Sketch020
  ArcFitTolerance = 1e-06
  AttachmentSupport = -> [Pocket017]
  ExternalGeometry = -> [Pocket017]
  ExternalTypes = [0]
  FullyConstrained = true
  MakeInternals = false
  MapMode = 5
  Placement = pos=(0,0,-10) rot=(1,0,0;3.14159rad)
  _ExternalGeoVersion = 0
  sketch-geometry (1):
    g0: Circle CenterX=55.6066 CenterY=-33.1066 CenterZ=0 NormalX=0 NormalY=0 NormalZ=1 AngleXU=0 Radius=7.5
  constraints (2):
    c: Diameter(g0) = 15
    c: Coincident(g0,g-3)
FEATURE [PartDesign::Pocket] Pocket018
  BaseFeature = -> Pocket017
  Direction = (0,0,1)
  Length = 1.55
  Length2 = 5
  Profile = -> Sketch020
  ReferenceAxis = -> Sketch020 [N_Axis]
  Refine = true
  SideType = 0
  Suppressed = false
  Type = 0
  Type2 = 0
FEATURE [Sketcher::SketchObject] Sketch033
  ArcFitTolerance = 1e-06
  AttachmentSupport = -> [XY_Plane005]
  ExternalGeometry = -> [Pocket018]
  ExternalTypes = [0]
  FullyConstrained = true
  MakeInternals = false
  MapMode = 5
  _ExternalGeoVersion = 0
  sketch-geometry (3):
    g0: LineSegment StartX=-62 StartY=-32.5005 StartZ=0 EndX=-62 EndY=15.0118 EndZ=0
    g1: ArcOfCircle CenterX=-42 CenterY=15.0118 CenterZ=0 NormalX=0 NormalY=0 NormalZ=1 AngleXU=0 Radius=20 StartAngle=1.5708 EndAngle=3.14159
    g2: LineSegment StartX=-42 StartY=35.0118 StartZ=0 EndX=48.4962 EndY=35.0118 EndZ=0
  constraints (7):
    c: Vertical(g0)
    c: Tangent(g0,g1) = 1.5708
    c: Tangent(g1,g2) = 1.5708
    c: Horizontal(g2)
    c: Equal(g-5,g1)
    c: Symmetric(g-6,g-6,g2)
    c: Symmetric(g-4,g-3,g0)
FEATURE [Sketcher::SketchObject] Sketch034
  ArcFitTolerance = 1e-06
  AttachmentOffset = pos=(0,0,-10) rot=(0,0,1;0rad)
  AttachmentSupport = -> [Pocket018]
  ExternalGeometry = -> [Pocket018]
  ExternalTypes = [0]
  FullyConstrained = true
  MakeInternals = false
  MapMode = 5
  Placement = pos=(0,-32.5,-2.2e-15) rot=(1,0,0;1.5708rad)
  _ExternalGeoVersion = 0
  sketch-geometry (4):
    g0: LineSegment StartX=-65 StartY=-2 StartZ=0 EndX=-59 EndY=-2 EndZ=0
    g1: LineSegment StartX=-59 StartY=-2 StartZ=0 EndX=-59 EndY=2 EndZ=0
    g2: LineSegment StartX=-59 StartY=2 StartZ=0 EndX=-65 EndY=2 EndZ=0
    g3: LineSegment StartX=-65 StartY=2 StartZ=0 EndX=-65 EndY=-2 EndZ=0
  constraints (10):
    c: Coincident(g0,g1)
    c: Coincident(g1,g2)
    c: Coincident(g2,g3)
    c: Coincident(g3,g0)
    c: Horizontal(g0)
    c: Horizontal(g2)
    c: Vertical(g1)
    c: Vertical(g3)
    c: Coincident(g0,g-6)
    c: Coincident(g1,g-3)
FEATURE [Sketcher::SketchObject] Sketch035
  ArcFitTolerance = 1e-06
  AttachmentSupport = -> [Pocket018]
  ExternalGeometry = -> [Sketch034,Sketch033,Pocket018]
  ExternalTypes = [0]
  FullyConstrained = true
  MakeInternals = false
  MapMode = 5
  Placement = pos=(36.4946,-9.77871,0) rot=(0.677661,0.519988,0.519988;1.95044rad)
  _ExternalGeoVersion = 0
  sketch-geometry (5):
    g0: LineSegment StartX=42.1206 StartY=-2 StartZ=0 EndX=50.6206 EndY=-2 EndZ=0
    g1: LineSegment StartX=50.6206 StartY=-2 StartZ=0 EndX=50.6206 EndY=2 EndZ=0
    g2: LineSegment StartX=50.6206 StartY=2 StartZ=0 EndX=42.1206 EndY=2 EndZ=0
    g3: GeomPoint [constr] X=46.3706 Y=3.6e-15 Z=0
    g4: LineSegment StartX=42.1206 StartY=2 StartZ=0 EndX=42.1206 EndY=-2 EndZ=0
  constraints (12):
    c: Coincident(g0,g1)
    c: Coincident(g1,g2)
    c: Horizontal(g0)
    c: Horizontal(g2)
    c: Vertical(g1)
    c: Symmetric(g2,g0,g3)
    c: Coincident(g3,g-5)
    c: Horizontal(g-3,g0)
    c: Coincident(g4,g2)
    c: Coincident(g4,g0)
    c: Vertical(g4)
    c: PointOnObject(g2,g-6)
FEATURE [PartDesign::SubtractivePipe] SubtractivePipe
  AuxiliaryCurvilinear = true
  AuxiliarySpineTangent = false
  BaseFeature = -> Pocket018
  Binormal = (0,0,0)
  Mode = 0
  Profile = -> Sketch034
  Refine = true
  Sections = -> [Sketch035]
  Spine = -> Sketch033
  SpineTangent = false
  Suppressed = false
  Transformation = 1
  Transition = 0
FEATURE [Sketcher::SketchObject] Sketch036
  ArcFitTolerance = 1e-06
  AttachmentSupport = -> [XY_Plane005]
  ExternalGeometry = -> [SubtractivePipe]
  ExternalTypes = [0]
  FullyConstrained = true
  MakeInternals = false
  MapMode = 5
  _ExternalGeoVersion = 0
  sketch-geometry (1):
    g0: LineSegment StartX=57.5118 StartY=25.9962 StartZ=0 EndX=62 EndY=-32.3815 EndZ=0
  constraints (2):
    c: Symmetric(g-3,g-3,g0)
    c: Symmetric(g-4,g-4,g0)
FEATURE [Sketcher::SketchObject] Sketch037
  ArcFitTolerance = 1e-06
  AttachmentOffset = pos=(0,0,-10) rot=(0,0,1;0rad)
  AttachmentSupport = -> [SubtractivePipe]
  ExternalGeometry = -> [SubtractivePipe,Sketch036]
  ExternalTypes = [0]
  FullyConstrained = true
  MakeInternals = false
  MapMode = 5
  Placement = pos=(0,-32.5,-2.2e-15) rot=(1,0,0;1.5708rad)
  _ExternalGeoVersion = 0
  sketch-geometry (5):
    g0: LineSegment StartX=65 StartY=-2 StartZ=0 EndX=65 EndY=2 EndZ=0
    g1: LineSegment StartX=65 StartY=2 StartZ=0 EndX=59 EndY=2 EndZ=0
    g2: LineSegment StartX=59 StartY=2 StartZ=0 EndX=59 EndY=-2 EndZ=0
    g3: LineSegment StartX=59 StartY=-2 StartZ=0 EndX=65 EndY=-2 EndZ=0
    g4: GeomPoint [constr] X=62 Y=0 Z=0
  constraints (11):
    c: Coincident(g0,g1)
    c: Coincident(g1,g2)
    c: Coincident(g2,g3)
    c: Coincident(g3,g0)
    c: Vertical(g0)
    c: Vertical(g2)
    c: Horizontal(g1)
    c: Horizontal(g3)
    c: Symmetric(g2,g0,g4)
    c: Coincident(g4,g-5)
    c: Coincident(g1,g-3)
FEATURE [Sketcher::SketchObject] Sketch038
  ArcFitTolerance = 1e-06
  AttachmentSupport = -> [SubtractivePipe]
  ExternalGeometry = -> [Sketch036,SubtractivePipe]
  ExternalTypes = [0]
  FullyConstrained = true
  MakeInternals = false
  MapMode = 5
  Placement = pos=(-2.64649,9.87684,0) rot=(-0.092692,0.704063,0.704063;3.32645rad)
  _ExternalGeoVersion = 0
  sketch-geometry (5):
    g0: LineSegment StartX=-66.5305 StartY=-2 StartZ=0 EndX=-58.0305 EndY=-2 EndZ=0
    g1: LineSegment StartX=-58.0305 StartY=-2 StartZ=0 EndX=-58.0305 EndY=2 EndZ=0
    g2: LineSegment StartX=-58.0305 StartY=2 StartZ=0 EndX=-66.5305 EndY=2 EndZ=0
    g3: LineSegment StartX=-66.5305 StartY=2 StartZ=0 EndX=-66.5305 EndY=-2 EndZ=0
    g4: GeomPoint [constr] X=-62.2805 Y=0 Z=0
  constraints (12):
    c: Coincident(g0,g1)
    c: Coincident(g1,g2)
    c: Coincident(g2,g3)
    c: Coincident(g3,g0)
    c: Horizontal(g0)
    c: Horizontal(g2)
    c: Vertical(g1)
    c: Vertical(g3)
    c: Symmetric(g2,g0,g4)
    c: Coincident(g4,g-5)
    c: PointOnObject(g2,g-6)
    c: Horizontal(g1,g-3)
FEATURE [PartDesign::SubtractivePipe] SubtractivePipe001
  AuxiliaryCurvilinear = true
  AuxiliarySpineTangent = false
  BaseFeature = -> SubtractivePipe
  Binormal = (0,0,0)
  Mode = 0
  Profile = -> Sketch037
  Refine = true
  Sections = -> [Sketch038]
  Spine = -> Sketch036
  SpineTangent = false
  Suppressed = false
  Transformation = 1
  Transition = 0
FEATURE [Sketcher::SketchObject] Sketch039
  ArcFitTolerance = 1e-06
  AttachmentSupport = -> [SubtractivePipe001]
  ExternalGeometry = -> [SubtractivePipe001]
  ExternalTypes = [0]
  FullyConstrained = true
  MakeInternals = false
  MapMode = 5
  Placement = pos=(0,47.5,0) rot=(0,0.707107,0.707107;3.14159rad)
  _ExternalGeoVersion = 0
  sketch-geometry (2):
    g0: Circle CenterX=58.3 CenterY=0 CenterZ=0 NormalX=0 NormalY=0 NormalZ=1 AngleXU=0 Radius=1.7
    g1: Circle CenterX=58.3 CenterY=0 CenterZ=0 NormalX=0 NormalY=0 NormalZ=1 AngleXU=0 Radius=1.5
  constraints (5):
    c: PointOnObject(g0,g-1)
    c: Coincident(g1,g0)
    c: Diameter(g1) = 3
    c: Diameter(g0) = 3.4
    c: Tangent(g0,g-3)
FEATURE [Sketcher::SketchObject] Sketch040
  ArcFitTolerance = 1e-06
  AttachmentSupport = -> [SubtractivePipe001]
  ExternalGeometry = -> [SubtractivePipe001]
  ExternalTypes = [0]
  FullyConstrained = true
  MakeInternals = false
  MapMode = 5
  Placement = pos=(-70,0,0) rot=(0.57735,-0.57735,-0.57735;2.0944rad)
  _ExternalGeoVersion = 0
  sketch-geometry (2):
    g0: Circle CenterX=-35.8 CenterY=0 CenterZ=0 NormalX=0 NormalY=0 NormalZ=1 AngleXU=0 Radius=1.7
    g1: Circle CenterX=-35.8 CenterY=0 CenterZ=0 NormalX=0 NormalY=0 NormalZ=1 AngleXU=0 Radius=1.5
  constraints (5):
    c: PointOnObject(g0,g-1)
    c: Coincident(g1,g0)
    c: Diameter(g1) = 3
    c: Diameter(g0) = 3.4
    c: Tangent(g0,g-3)
FEATURE [PartDesign::Pocket] Pocket019
  BaseFeature = -> SubtractivePipe001
  Direction = (0,-1,2e-16)
  Length = 9
  Length2 = 5
  Profile = -> Sketch039 [Edge2]
  ReferenceAxis = -> Sketch039 [N_Axis]
  Refine = true
  SideType = 0
  Suppressed = false
  Type = 0
  Type2 = 0
FEATURE [PartDesign::Pocket] Pocket020
  BaseFeature = -> Pocket019
  Direction = (0,-1,2e-16)
  Length = 8
  Length2 = 5
  Profile = -> Sketch039 [Edge1]
  ReferenceAxis = -> Sketch039 [N_Axis]
  Refine = true
  SideType = 0
  Suppressed = false
  Type = 0
  Type2 = 0
FEATURE [PartDesign::Pocket] Pocket021
  BaseFeature = -> Pocket020
  Direction = (1,0,0)
  Length = 9
  Length2 = 5
  Profile = -> Sketch040 [Edge2]
  ReferenceAxis = -> Sketch040 [N_Axis]
  Refine = true
  SideType = 0
  Suppressed = false
  Type = 0
  Type2 = 0
FEATURE [PartDesign::Pocket] Pocket022
  BaseFeature = -> Pocket021
  Direction = (1,0,0)
  Length = 8
  Length2 = 5
  Profile = -> Sketch040 [Edge1]
  ReferenceAxis = -> Sketch040 [N_Axis]
  Refine = true
  SideType = 0
  Suppressed = false
  Type = 0
  Type2 = 0
FEATURE [PartDesign::Fillet] Fillet004
  Base = -> Pocket022 [Edge59,Edge80]
  BaseFeature = -> Pocket022
  Radius = 5
  Refine = true
  SupportTransform = false
  Suppressed = false
  UseAllEdges = false
FEATURE [PartDesign::Body] Body004  label="IrSensor"
  AllowCompound = false
  Group = -> [Sketch016,Pad014,Sketch017,Pocket015,Pocket016,Mirrored006,Sketch019,Pocket017,Sketch020,Pocket018,Sketch033,Sketch034,Sketch035,SubtractivePipe,Sketch036,Sketch037,Sketch038,SubtractivePipe001,Sketch039,Sketch040,Pocket019,Pocket020,Pocket021,Pocket022,Fillet004]
  Origin = -> Origin005
  Tip = -> Fillet004
COMPONENT P5 — recipe-attached ("Knob001", modeled in this document).
Construction recipe (the document's own serialized feature program — sketch geometry with constraints, then the solid features built on it; lengths are millimeters unless a unit is written):

FEATURE [Sketcher::SketchObject] Sketch052
  ArcFitTolerance = 1e-06
  AttachmentSupport = -> [XY_Plane009]
  ExternalTypes = [0]
  FullyConstrained = true
  MakeInternals = false
  MapMode = 5
  _ExternalGeoVersion = 0
  sketch-geometry (5):
    g0: ArcOfCircle CenterX=0 CenterY=0 CenterZ=0 NormalX=0 NormalY=0 NormalZ=1 AngleXU=0 Radius=3 StartAngle=2.49809 EndAngle=6.92669
    g1: LineSegment StartX=-2.4 StartY=1.8 StartZ=0 EndX=2.4 EndY=1.8 EndZ=0
    g2: GeomPoint X=0 Y=-3 Z=0
    g3: Circle CenterX=0 CenterY=0 CenterZ=0 NormalX=0 NormalY=0 NormalZ=1 AngleXU=0 Radius=15
    g4: Circle CenterX=0 CenterY=0 CenterZ=0 NormalX=0 NormalY=0 NormalZ=1 AngleXU=0 Radius=11.5
  constraints (12):
    c: Diameter(g0) = 6
    c: Coincident(g0,g-1)
    c: Horizontal(g1)
    c: PointOnObject(g2,g0)
    c: PointOnObject(g2,g-2)
    c: DistanceY(g2,g1) = 4.8
    c: Coincident(g0,g1)
    c: Coincident(g0,g1)
    c: Diameter(g3) = 30
    c: Coincident(g3,g0)
    c: Coincident(g4,g0)
    c: Diameter(g4) = 23
FEATURE [PartDesign::Pad] Pad028
  Direction = (0,0,1)
  Length = 1
  Length2 = 10
  Profile = -> Sketch052 [Edge3]
  ReferenceAxis = -> Sketch052 [N_Axis]
  Refine = true
  Reversed = true
  SideType = 0
  Suppressed = false
  Type = 0
  Type2 = 0
FEATURE [PartDesign::Pad] Pad029
  BaseFeature = -> Pad028
  Direction = (0,0,1)
  Length = 7
  Length2 = 10
  Profile = -> Sketch052 [Edge3,Edge1,Edge2]
  ReferenceAxis = -> Sketch052 [N_Axis]
  Refine = true
  SideType = 0
  Suppressed = false
  Type = 0
  Type2 = 0
FEATURE [PartDesign::Pad] Pad030
  BaseFeature = -> Pad029
  Direction = (0,0,1)
  Length = 14
  Length2 = 10
  Profile = -> Sketch052 [Edge4,Edge3]
  ReferenceAxis = -> Sketch052 [N_Axis]
  Refine = true
  SideType = 0
  Suppressed = false
  Type = 0
  Type2 = 0
FEATURE [Sketcher::SketchObject] Sketch053
  ArcFitTolerance = 1e-06
  AttachmentSupport = -> [Pad030]
  ExternalGeometry = -> [Sketch052]
  ExternalTypes = [0]
  FullyConstrained = true
  MakeInternals = false
  MapMode = 5
  Placement = pos=(0,0,-1) rot=(1,0,0;3.14159rad)
  _ExternalGeoVersion = 0
  sketch-geometry (2):
    g0: ArcOfCircle CenterX=0 CenterY=15 CenterZ=0 NormalX=0 NormalY=0 NormalZ=1 AngleXU=0 Radius=1.5 StartAngle=3.19161 EndAngle=6.23316
    g1: ArcOfCircle CenterX=0 CenterY=0 CenterZ=0 NormalX=0 NormalY=0 NormalZ=1 AngleXU=0 Radius=15 StartAngle=1.47075 EndAngle=1.67084
  constraints (7):
    c: PointOnObject(g0,g-2)
    c: PointOnObject(g0,g-3)
    c: PointOnObject(g0,g-3)
    c: Coincident(g1,g-1)
    c: Coincident(g1,g0)
    c: Coincident(g1,g0)
    c: Radius(g0) = 1.5
FEATURE [PartDesign::Pocket] Pocket026
  BaseFeature = -> Pad030
  Direction = (0,0,1)
  Length = 5
  Length2 = 5
  Profile = -> Sketch053
  ReferenceAxis = -> Sketch053 [N_Axis]
  Refine = true
  SideType = 0
  Suppressed = false
  Type = 1
  Type2 = 0
FEATURE [PartDesign::Fillet] Fillet005
  Base = -> Pocket026 [Edge4,Edge2,Edge6,Edge1]
  BaseFeature = -> Pocket026
  Radius = 1
  Refine = true
  SupportTransform = false
  Suppressed = false
  UseAllEdges = false
FEATURE [PartDesign::PolarPattern] PolarPattern001
  Angle = 360
  Axis = -> Sketch053 [N_Axis]
  BaseFeature = -> Fillet005
  Mode = 0
  Occurrences = 10
  Offset = 120
  Originals = -> [Pocket026,Fillet005]
  Refine = true
  SpacingPattern = [0]
  Spacings = [-1,-1,-1,-1,-1,-1,-1,-1,-1]
  Suppressed = false
  TransformMode = 0
FEATURE [Sketcher::SketchObject] Sketch054
  ArcFitTolerance = 1e-06
  AttachmentSupport = -> [PolarPattern001]
  ExternalGeometry = -> [Sketch052]
  ExternalTypes = [0]
  FullyConstrained = true
  MakeInternals = false
  MapMode = 5
  Placement = pos=(0,0,-1) rot=(1,0,0;3.14159rad)
  _ExternalGeoVersion = 0
  sketch-geometry (25):
    g0: ArcOfCircle CenterX=0 CenterY=0 CenterZ=0 NormalX=0 NormalY=0 NormalZ=1 AngleXU=0 Radius=11 StartAngle=1.74533 EndAngle=3.14159
    g1: ArcOfCircle CenterX=0 CenterY=0 CenterZ=0 NormalX=0 NormalY=0 NormalZ=1 AngleXU=0 Radius=8 StartAngle=1.74533 EndAngle=3.14159
    g2: LineSegment StartX=-11 StartY=-2.7e-15 StartZ=0 EndX=-13 EndY=-3.2e-15 EndZ=0
    g3: LineSegment StartX=-8 StartY=0 StartZ=0 EndX=-6 EndY=-1.5e-15 EndZ=0
    g4: LineSegment StartX=-6 StartY=-1.5e-15 StartZ=0 EndX=-9.5 EndY=-5.48483 EndZ=0
    g5: LineSegment StartX=-13 StartY=-3.2e-15 StartZ=0 EndX=-9.5 EndY=-5.48483 EndZ=0
    g6: LineSegment StartX=-1.38919 StartY=7.87846 StartZ=0 EndX=-1.91013 EndY=10.8329 EndZ=0
    g7: LineSegment [constr] StartX=-8 StartY=0 StartZ=0 EndX=-11 EndY=-2.7e-15 EndZ=0
    g8: LineSegment [constr] StartX=-10.799 StartY=-6.23483 StartZ=0 EndX=-8.20096 EndY=-4.73483 EndZ=0
    g9: ArcOfCircle CenterX=0 CenterY=0 CenterZ=0 NormalX=0 NormalY=0 NormalZ=1 AngleXU=0 Radius=11 StartAngle=0 EndAngle=1.39626
    g10: ArcOfCircle CenterX=0 CenterY=0 CenterZ=0 NormalX=0 NormalY=0 NormalZ=1 AngleXU=0 Radius=8 StartAngle=0 EndAngle=1.39626
    g11: LineSegment StartX=11 StartY=0 StartZ=0 EndX=13 EndY=-3.2e-15 EndZ=0
    g12: LineSegment StartX=8 StartY=0 StartZ=0 EndX=6 EndY=-1.5e-15 EndZ=0
    g13: LineSegment StartX=6 StartY=-1.5e-15 StartZ=0 EndX=9.5 EndY=-5.48483 EndZ=0
    g14: LineSegment StartX=13 StartY=-3.2e-15 StartZ=0 EndX=9.5 EndY=-5.48483 EndZ=0
    g15: LineSegment StartX=1.38919 StartY=7.87846 StartZ=0 EndX=1.91013 EndY=10.8329 EndZ=0
    g16: LineSegment [constr] StartX=8 StartY=0 StartZ=0 EndX=11 EndY=0 EndZ=0
    g17: LineSegment [constr] StartX=10.799 StartY=-6.23483 StartZ=0 EndX=8.20096 EndY=-4.73483 EndZ=0
    g18: LineSegment StartX=4 StartY=-2 StartZ=0 EndX=-4 EndY=-2 EndZ=0
    g19: LineSegment StartX=-4 StartY=-2 StartZ=0 EndX=0 EndY=-6.47214 EndZ=0
    g20: LineSegment StartX=0 StartY=-6.47214 StartZ=0 EndX=4 EndY=-2 EndZ=0
    g21: LineSegment StartX=-4.5 StartY=-8.47214 StartZ=0 EndX=-4.5 EndY=-10.4721 EndZ=0
    g22: LineSegment StartX=-4.5 StartY=-10.4721 StartZ=0 EndX=4.5 EndY=-10.4721 EndZ=0
    g23: LineSegment StartX=4.5 StartY=-10.4721 StartZ=0 EndX=4.5 EndY=-8.47214 EndZ=0
    g24: LineSegment StartX=4.5 StartY=-8.47214 StartZ=0 EndX=-4.5 EndY=-8.47214 EndZ=0
  constraints (71):
    c: Coincident(g0,g-1)
    c: Coincident(g1,g0)
    c: Coincident(g2,g0)
    c: Coincident(g3,g1)
    c: Coincident(g4,g3)
    c: Coincident(g5,g2)
    c: Coincident(g5,g4)
    c: Perpendicular(g-3,g2)
    c: Perpendicular(g-3,g3)
    c: Equal(g4,g5)
    c: Coincident(g6,g1)
    c: Coincident(g6,g0)
    c: Perpendicular(g0,g6)
    c: Equal(g2,g3)
    c: Coincident(g7,g1)
    c: Coincident(g7,g0)
    c: Perpendicular(g-3,g7)
    c: Equal(g8,g6)
    c: Perpendicular(g-3,g8)
    c: Symmetric(g8,g8,g4)
    c: Angle(g6,g8) = 1.91986
    c: Angle(g7,g8) = 0.523599
    c: Angle(g-2,g6) = 0.174533
    c: Coincident(g10,g9)
    c: Coincident(g11,g9)
    c: Coincident(g12,g10)
    c: Coincident(g13,g12)
    c: Coincident(g14,g11)
    c: Coincident(g14,g13)
    c: Equal(g13,g14)
    c: Coincident(g15,g10)
    c: Coincident(g15,g9)
    c: Perpendicular(g9,g15)
    c: Equal(g11,g12)
    c: Coincident(g16,g10)
    c: Coincident(g16,g9)
    c: Equal(g17,g15)
    c: Symmetric(g17,g17,g13)
    c: Perpendicular(g-3,g11)
    c: Perpendicular(g-3,g12)
    c: Perpendicular(g-3,g17)
    c: Coincident(g9,g0)
    c: Perpendicular(g-3,g16)
    c: Horizontal(g0,g9)
    c: Horizontal(g18)
    c: Coincident(g18,g19)
    c: Coincident(g19,g20)
    c: Coincident(g20,g18)
    c: Equal(g20,g19)
    c: Coincident(g21,g22)
    c: Coincident(g22,g23)
    c: Coincident(g23,g24)
    c: Coincident(g24,g21)
    c: Vertical(g21)
    c: Vertical(g23)
    c: Horizontal(g24)
    c: Symmetric(g21,g22,g-2)
    c: DistanceY(g23,g19) = 2
    c: DistanceX(g21,g18) = 0.5
    c: Equal(g2,g11)
    c: Distance(g6,g6) = 3
    c: Horizontal(g1,g10)
    c: Horizontal(g13,g4)
    c: Symmetric(g1,g10,g-2)
    c: DistanceY(g23,g23) = 2
    c: DistanceX(g11,g11) = 2
    c: DistanceX(g18,g18) = 8
    c: Distance(g20,g20) = 6
    c: Radius(g1) = 8
    c: PointOnObject(g19,g-2)
    c: DistanceY(g18,g-1) = 2
FEATURE [PartDesign::Pocket] Pocket027
  BaseFeature = -> PolarPattern001
  Direction = (0,0,1)
  Length = 0.4
  Length2 = 5
  Profile = -> Sketch054
  ReferenceAxis = -> Sketch054 [N_Axis]
  Refine = true
  SideType = 0
  Suppressed = false
  Type = 0
  Type2 = 0
FEATURE [PartDesign::Body] Body008  label="Knob"
  AllowCompound = false
  Group = -> [Sketch052,Sketch053,Sketch054,Pad028,Pad029,Pad030,Pocket026,Fillet005,PolarPattern001,Pocket027]
  Origin = -> Origin009
  Tip = -> Pocket027
COMPONENT P6 — geometry summary ("M3-Nut001"; no construction recipe available for this part):
  bounding box: 6.4 x 5.5 x 2.4 mm
  tessellated surface: 2,120 triangles
  volume: 51 mm^3 (60% of its bounding box)
  symmetry: 2-fold rotationally symmetric about the x axis; 6-fold rotationally symmetric about the y axis; mirror-symmetric across its x mid-plane, y mid-plane, z mid-plane
COMPONENT P7 — geometry summary ("M3-Nut002"; no construction recipe available for this part):
  bounding box: 6.4 x 5.5 x 2.4 mm
  tessellated surface: 2,120 triangles
  volume: 51 mm^3 (60% of its bounding box)
  symmetry: 2-fold rotationally symmetric about the x axis; 6-fold rotationally symmetric about the y axis; mirror-symmetric across its x mid-plane, y mid-plane, z mid-plane
COMPONENT P8 — geometry summary ("M3x16-Screw001"; no construction recipe available for this part):
  bounding box: 18.0 x 5.5 x 5.5 mm
  tessellated surface: 5,414 triangles
  volume: 153 mm^3 (28% of its bounding box)
  symmetry: revolution-symmetric about the x axis through its bounding-box center; mirror-symmetric across its y mid-plane, z mid-plane
COMPONENT P9 — geometry summary ("M3x16-Screw002"; no construction recipe available for this part):
  bounding box: 18.0 x 5.5 x 5.5 mm
  tessellated surface: 5,414 triangles
  volume: 153 mm^3 (28% of its bounding box)
  symmetry: revolution-symmetric about the x axis through its bounding-box center; mirror-symmetric across its y mid-plane, z mid-plane
COMPONENT P10 — recipe-attached ("Painel001", modeled in this document).
Construction recipe (the document's own serialized feature program — sketch geometry with constraints, then the solid features built on it; lengths are millimeters unless a unit is written):

FEATURE [Sketcher::SketchObject] Sketch001
  ArcFitTolerance = 1e-06
  AttachmentSupport = -> [XY_Plane001]
  ExternalTypes = [0]
  FullyConstrained = true
  MakeInternals = false
  MapMode = 5
  _ExternalGeoVersion = 0
  sketch-geometry (15):
    g0: LineSegment StartX=-62.65 StartY=-36.55 StartZ=0 EndX=62.65 EndY=-36.55 EndZ=0
    g1: LineSegment StartX=62.65 StartY=-36.55 StartZ=0 EndX=62.65 EndY=36.55 EndZ=0
    g2: LineSegment StartX=62.65 StartY=36.55 StartZ=0 EndX=-62.65 EndY=36.55 EndZ=0
    g3: LineSegment StartX=-62.65 StartY=36.55 StartZ=0 EndX=-62.65 EndY=-36.55 EndZ=0
    g4: GeomPoint [constr] X=0 Y=0 Z=0
    g5: LineSegment StartX=-62.65 StartY=-39.55 StartZ=0 EndX=62.65 EndY=-39.55 EndZ=0
    g6: LineSegment StartX=65.65 StartY=-36.55 StartZ=0 EndX=65.65 EndY=36.55 EndZ=0
    g7: LineSegment StartX=62.65 StartY=39.55 StartZ=0 EndX=-62.65 EndY=39.55 EndZ=0
    g8: LineSegment StartX=-65.65 StartY=36.55 StartZ=0 EndX=-65.65 EndY=-36.55 EndZ=0
    g9: ArcOfCircle CenterX=-62.65 CenterY=-36.55 CenterZ=0 NormalX=0 NormalY=0 NormalZ=1 AngleXU=0 Radius=3 StartAngle=3.14159 EndAngle=4.71239
    g10: ArcOfCircle CenterX=62.65 CenterY=-36.55 CenterZ=0 NormalX=0 NormalY=0 NormalZ=1 AngleXU=0 Radius=3 StartAngle=4.71239 EndAngle=6.28319
    g11: ArcOfCircle CenterX=62.65 CenterY=36.55 CenterZ=0 NormalX=0 NormalY=0 NormalZ=1 AngleXU=0 Radius=3 StartAngle=0 EndAngle=1.5708
    g12: ArcOfCircle CenterX=-62.65 CenterY=36.55 CenterZ=0 NormalX=0 NormalY=0 NormalZ=1 AngleXU=0 Radius=3 StartAngle=1.5708 EndAngle=3.14159
    g13: GeomPoint [constr] X=-65.65 Y=-39.55 Z=0
    g14: GeomPoint [constr] X=65.65 Y=39.55 Z=0
  constraints (35):
    c: Coincident(g0,g1)
    c: Coincident(g1,g2)
    c: Coincident(g2,g3)
    c: Coincident(g3,g0)
    c: Horizontal(g0)
    c: Horizontal(g2)
    c: Vertical(g1)
    c: Vertical(g3)
    c: Symmetric(g2,g0,g4)
    c: Distance(g1,g3) = 125.3  'display_inner_length'
    c: Coincident(g4,g-1)
    c: DistanceY(g3,g3) = 73.1  'display_inner_width'
    c: Tangent(g5,g9) = -1.5708
    c: Tangent(g5,g10) = -1.5708
    c: Tangent(g6,g10) = -1.5708
    c: Tangent(g6,g11) = -1.5708
    c: Tangent(g7,g11) = -1.5708
    c: Tangent(g7,g12) = -1.5708
    c: Tangent(g8,g12) = -1.5708
    c: Tangent(g8,g9) = -1.5708
    c: Horizontal(g5)
    c: Horizontal(g7)
    c: Vertical(g6)
    c: Vertical(g8)
    c: Equal(g9,g10)
    c: Equal(g10,g11)
    c: Equal(g11,g12)
    c: PointOnObject(g13,g5)
    c: PointOnObject(g13,g8)
    c: PointOnObject(g14,g6)
    c: PointOnObject(g14,g7)
    c: Symmetric(g13,g14,g4)
    c: Radius(g11) = 3
    c: Distance(g1,g7) = 3
    c: DistanceX(g1,g6) = 3
FEATURE [PartDesign::Pad] Pad
  Direction = (0,0,1)
  Length = 3
  Length2 = 10
  Profile = -> Sketch001 [Edge11,Edge12,Edge5,Edge9,Edge10,Edge7,Edge8,Edge6]
  ReferenceAxis = -> Sketch001 [N_Axis]
  Refine = true
  SideType = 0
  Suppressed = false
  Type = 0
  Type2 = 0
FEATURE [PartDesign::Pad] Pad001
  BaseFeature = -> Pad
  Direction = (0,0,1)
  Length = 30
  Length2 = 10
  Profile = -> Sketch001
  ReferenceAxis = -> Sketch001 [N_Axis]
  Refine = true
  SideType = 0
  Suppressed = false
  Type = 0
  Type2 = 0
FEATURE [Sketcher::SketchObject] Sketch002
  ArcFitTolerance = 1e-06
  AttachmentSupport = -> [Pad001]
  ExternalGeometry = -> [Pad001]
  ExternalTypes = [0]
  FullyConstrained = true
  MakeInternals = false
  MapMode = 5
  Placement = pos=(0,0,0) rot=(1,0,0;3.14159rad)
  _ExternalGeoVersion = 0
  sketch-geometry (19):
    g0: LineSegment [constr] StartX=-59.65 StartY=30 StartZ=0 EndX=38.35 EndY=30 EndZ=0
    g1: LineSegment [constr] StartX=38.35 StartY=30 StartZ=0 EndX=38.35 EndY=-30 EndZ=0
    g2: LineSegment [constr] StartX=38.35 StartY=-30 StartZ=0 EndX=-59.65 EndY=-30 EndZ=0
    g3: LineSegment [constr] StartX=-59.65 StartY=-30 StartZ=0 EndX=-59.65 EndY=30 EndZ=0
    g4: LineSegment [constr] StartX=40.45 StartY=-1.85 StartZ=0 EndX=59.65 EndY=-1.85 EndZ=0
    g5: LineSegment [constr] StartX=59.65 StartY=-1.85 StartZ=0 EndX=59.65 EndY=-23.25 EndZ=0
    g6: LineSegment [constr] StartX=59.65 StartY=-23.25 StartZ=0 EndX=40.45 EndY=-23.25 EndZ=0
    g7: LineSegment [constr] StartX=40.45 StartY=-23.25 StartZ=0 EndX=40.45 EndY=-1.85 EndZ=0
    g8: LineSegment [constr] StartX=42.3 StartY=-6.65 StartZ=0 EndX=54.2 EndY=-6.65 EndZ=0
    g9: LineSegment [constr] StartX=54.2 StartY=-6.65 StartZ=0 EndX=54.2 EndY=-18.55 EndZ=0
    g10: LineSegment [constr] StartX=54.2 StartY=-18.55 StartZ=0 EndX=42.3 EndY=-18.55 EndZ=0
    g11: LineSegment [constr] StartX=42.3 StartY=-18.55 StartZ=0 EndX=42.3 EndY=-6.65 EndZ=0
    g12: Circle CenterX=48.25 CenterY=-12.6 CenterZ=0 NormalX=0 NormalY=0 NormalZ=1 AngleXU=0 Radius=3.475
    g13: LineSegment StartX=-48.65 StartY=12.6 StartZ=0 EndX=27.35 EndY=12.6 EndZ=0
    g14: LineSegment StartX=27.35 StartY=12.6 StartZ=0 EndX=27.35 EndY=-12.6 EndZ=0
    g15: LineSegment StartX=27.35 StartY=-12.6 StartZ=0 EndX=-48.65 EndY=-12.6 EndZ=0
    g16: LineSegment StartX=-48.65 StartY=-12.6 StartZ=0 EndX=-48.65 EndY=12.6 EndZ=0
    g17: GeomPoint [constr] X=-10.65 Y=0 Z=0
    g18: GeomPoint [constr] X=48.25 Y=-9.125 Z=0
  constraints (52):
    c: Coincident(g0,g1)
    c: Coincident(g1,g2)
    c: Coincident(g2,g3)
    c: Coincident(g3,g0)
    c: Horizontal(g0)
    c: Horizontal(g2)
    c: Vertical(g1)
    c: Vertical(g3)
    c: Coincident(g4,g5)
    c: Coincident(g5,g6)
    c: Coincident(g6,g7)
    c: Coincident(g7,g4)
    c: Horizontal(g4)
    c: Horizontal(g6)
    c: Vertical(g5)
    c: Vertical(g7)
    c: Coincident(g8,g9)
    c: Coincident(g9,g10)
    c: Coincident(g10,g11)
    c: Coincident(g11,g8)
    c: Horizontal(g8)
    c: Horizontal(g10)
    c: Vertical(g9)
    c: Vertical(g11)
    c: Coincident(g13,g14)
    c: Coincident(g14,g15)
    c: Coincident(g15,g16)
    c: Coincident(g16,g13)
    c: Horizontal(g13)
    c: Horizontal(g15)
    c: Vertical(g14)
    c: Vertical(g16)
    c: Distance(g2) = 98
    c: Distance(g1) = 60
    c: Distance(g15) = 76
    c: Distance(g14) = 25.2
    c: Symmetric(g0,g1,g17)
    c: Symmetric(g13,g14,g17)
    c: Distance(g6) = 19.2
    c: Distance(g5) = 21.4
    c: Distance(g10) = 11.9
    c: Distance(g9) = 11.9
    c: Diameter(g12) = 6.95
    c: Symmetric(g8,g9,g12)
    c: DistanceY(g5,g9) = 4.7
    c: DistanceX(g9,g5) = 5.45
    c: PointOnObject(g18,g12)
    c: Vertical(g12,g18)
    c: Horizontal(g17,g-1)
    c: Horizontal(g12,g14)
    c: DistanceX(g-3,g2) = 6
    c: DistanceX(g4,g-4) = 6
FEATURE [PartDesign::Pocket] Pocket
  BaseFeature = -> Pad001
  Direction = (0,0,1)
  Length = 5
  Length2 = 5
  Profile = -> Sketch002
  ReferenceAxis = -> Sketch002 [N_Axis]
  Refine = true
  SideType = 0
  Suppressed = false
  Type = 1
  Type2 = 0
FEATURE [PartDesign::Plane] DatumPlane
  AttachmentSupport = -> [Pocket]
  Length = 99.4822
  MapMode = 45
  Placement = pos=(-10.65,1.8e-15,3) rot=(0,0,1;1.5708rad)
  ResizeMode = 0
  Width = 151.682
FEATURE [Sketcher::SketchObject] Sketch003
  ArcFitTolerance = 1e-06
  AttachmentOffset = pos=(0,0,9.4) rot=(0,0,1;0rad)
  AttachmentSupport = -> [DatumPlane]
  ExternalTypes = [0]
  FullyConstrained = true
  MakeInternals = false
  MapMode = 5
  Placement = pos=(-10.65,1.8e-15,12.4) rot=(0,0,1;1.5708rad)
  _ExternalGeoVersion = 0
  sketch-geometry (3):
    g0: Circle CenterX=-27.5 CenterY=46.5 CenterZ=0 NormalX=0 NormalY=0 NormalZ=1 AngleXU=0 Radius=4
    g1: Circle CenterX=-27.5 CenterY=46.5 CenterZ=0 NormalX=0 NormalY=0 NormalZ=1 AngleXU=0 Radius=1.7
    g2: Circle CenterX=-27.5 CenterY=46.5 CenterZ=0 NormalX=0 NormalY=0 NormalZ=1 AngleXU=0 Radius=1.5
  constraints (7):
    c: Coincident(g1,g0)
    c: DistanceX(g0,g-1) = 27.5
    c: DistanceY(g-1,g0) = 46.5
    c: Diameter(g0) = 8
    c: Diameter(g1) = 3.4
    c: Coincident(g2,g0)
    c: Diameter(g2) = 3
FEATURE [PartDesign::Pad] Pad002
  BaseFeature = -> Pocket
  Direction = (0,0,1)
  Length = 10
  Length2 = 10
  Profile = -> Sketch003 [Edge1]
  ReferenceAxis = -> Sketch003 [N_Axis]
  Refine = true
  Reversed = true
  SideType = 0
  Suppressed = false
  Type = 2
  Type2 = 0
FEATURE [PartDesign::Pocket] Pocket001
  BaseFeature = -> Pad002
  Direction = (0,0,-1)
  Length = 0
  Length2 = 5
  Profile = -> Sketch003 [Edge3]
  ReferenceAxis = -> Sketch003 [N_Axis]
  Refine = true
  SideType = 0
  Suppressed = false
  Type = 3
  Type2 = 0
  UpToFace = -> Pad002 [Face15]
FEATURE [PartDesign::Pocket] Pocket002
  BaseFeature = -> Pocket001
  Direction = (0,0,-1)
  Length = 4
  Length2 = 5
  Profile = -> Sketch003 [Edge2]
  ReferenceAxis = -> Sketch003 [N_Axis]
  Refine = true
  SideType = 0
  Suppressed = false
  Type = 0
  Type2 = 0
FEATURE [PartDesign::Mirrored] Mirrored
  MirrorPlane = -> Sketch003 [V_Axis]
  Refine = true
  Suppressed = false
  TransformMode = 0
FEATURE [PartDesign::Mirrored] Mirrored001
  MirrorPlane = -> Sketch003 [H_Axis]
  Refine = true
  Suppressed = false
  TransformMode = 0
FEATURE [PartDesign::MultiTransform] MultiTransform
  BaseFeature = -> Pocket002
  Originals = -> [Pad002,Pocket002,Pocket001]
  Refine = true
  Suppressed = false
  TransformMode = 0
  Transformations = -> [Mirrored,Mirrored001]
FEATURE [Sketcher::SketchObject] Sketch004
  ArcFitTolerance = 1e-06
  AttachmentSupport = -> [MultiTransform]
  ExternalGeometry = -> [MultiTransform]
  ExternalTypes = [0]
  FullyConstrained = true
  MakeInternals = false
  MapMode = 5
  Placement = pos=(0,0,3) rot=(0,0,1;0rad)
  _ExternalGeoVersion = 0
  sketch-geometry (2):
    g0: Circle CenterX=48.25 CenterY=-12.6 CenterZ=0 NormalX=0 NormalY=0 NormalZ=1 AngleXU=0 Radius=2.55
    g1: Circle CenterX=48.25 CenterY=-12.6 CenterZ=0 NormalX=0 NormalY=0 NormalZ=1 AngleXU=0 Radius=3.5
  constraints (5):
    c: Coincident(g1,g0)
    c: Horizontal(g-4,g0)
    c: Vertical(g0,g-3)
    c: Diameter(g0) = 5.1
    c: Diameter(g1) = 7
FEATURE [PartDesign::Pocket] Pocket003
  BaseFeature = -> MultiTransform
  Direction = (0,0,-1)
  Length = 5
  Length2 = 5
  Offset = -0.2
  Profile = -> Sketch004 [Edge1]
  ReferenceAxis = -> Sketch004 [N_Axis]
  Refine = true
  SideType = 0
  Suppressed = false
  Type = 2
  Type2 = 0
FEATURE [PartDesign::Pad] Pad003
  BaseFeature = -> Pocket003
  Direction = (0,0,1)
  Length = 1.2
  Length2 = 10
  Profile = -> Sketch004 [Edge2,Edge1]
  ReferenceAxis = -> Sketch004 [N_Axis]
  Refine = true
  SideType = 0
  Suppressed = false
  Type = 0
  Type2 = 0
FEATURE [Sketcher::SketchObject] Sketch005
  ArcFitTolerance = 1e-06
  AttachmentSupport = -> [YZ_Plane001]
  ExternalGeometry = -> [Pad003]
  ExternalTypes = [0]
  FullyConstrained = true
  MakeInternals = false
  MapMode = 5
  Placement = pos=(0,0,0) rot=(0.57735,0.57735,0.57735;2.0944rad)
  _ExternalGeoVersion = 0
  sketch-geometry (7):
    g0: LineSegment StartX=-39.55 StartY=19.5 StartZ=0 EndX=-10 EndY=19.5 EndZ=0
    g1: ArcOfCircle CenterX=0 CenterY=19.5 CenterZ=0 NormalX=0 NormalY=0 NormalZ=1 AngleXU=0 Radius=10 StartAngle=0 EndAngle=3.14159
    g2: LineSegment StartX=10 StartY=19.5 StartZ=0 EndX=39.55 EndY=19.5 EndZ=0
    g3: LineSegment StartX=39.55 StartY=19.5 StartZ=0 EndX=39.55 EndY=30 EndZ=0
    g4: LineSegment StartX=39.55 StartY=30 StartZ=0 EndX=-39.55 EndY=30 EndZ=0
    g5: LineSegment StartX=-39.55 StartY=30 StartZ=0 EndX=-39.55 EndY=19.5 EndZ=0
    g6: Circle CenterX=0 CenterY=19.5 CenterZ=0 NormalX=0 NormalY=0 NormalZ=1 AngleXU=0 Radius=1.5
  constraints (16):
    c: Horizontal(g0)
    c: Perpendicular(g0,g1) = 4.71239
    c: Perpendicular(g1,g2) = 4.71239
    c: Coincident(g2,g3)
    c: Vertical(g3)
    c: Coincident(g3,g4)
    c: Coincident(g4,g5)
    c: Coincident(g5,g0)
    c: Vertical(g5)
    c: Radius(g1) = 10
    c: Coincident(g4,g-3)
    c: Symmetric(g4,g3,g-2)
    c: Symmetric(g0,g2,g1)
    c: DistanceY(g5,g5) = 10.5
    c: Coincident(g6,g1)
    c: Diameter(g6) = 3
FEATURE [PartDesign::Pocket] Pocket004
  BaseFeature = -> Pad003
  Direction = (-1,0,0)
  Length = 5
  Length2 = 5
  Profile = -> Sketch005
  ReferenceAxis = -> Sketch005 [N_Axis]
  Refine = true
  SideType = 2
  Suppressed = false
  Type = 1
  Type2 = 0
FEATURE [PartDesign::Fillet] Fillet
  Base = -> Pocket004 [Edge77]
  BaseFeature = -> Pocket004
  Radius = 3
  Refine = true
  SupportTransform = false
  Suppressed = false
  UseAllEdges = false
FEATURE [Sketcher::SketchObject] Sketch006
  ArcFitTolerance = 1e-06
  AttachmentSupport = -> [Fillet]
  ExternalGeometry = -> [Fillet]
  ExternalTypes = [0]
  FullyConstrained = true
  MakeInternals = false
  MapMode = 5
  Placement = pos=(0,0,3) rot=(0,0,1;0rad)
  _ExternalGeoVersion = 0
  sketch-geometry (4):
    g0: LineSegment StartX=62.65 StartY=-36.55 StartZ=0 EndX=62.65 EndY=-33.55 EndZ=0
    g1: LineSegment StartX=62.65 StartY=-33.55 StartZ=0 EndX=59.65 EndY=-33.55 EndZ=0
    g2: LineSegment StartX=59.65 StartY=-33.55 StartZ=0 EndX=59.65 EndY=-36.55 EndZ=0
    g3: LineSegment StartX=59.65 StartY=-36.55 StartZ=0 EndX=62.65 EndY=-36.55 EndZ=0
  constraints (11):
    c: Coincident(g0,g1)
    c: Coincident(g1,g2)
    c: Coincident(g2,g3)
    c: Coincident(g3,g0)
    c: Vertical(g0)
    c: Vertical(g2)
    c: Horizontal(g1)
    c: Horizontal(g3)
    c: Distance(g0,g2) = 3
    c: Distance(g1,g3) = 3
    c: Coincident(g0,g-3)
FEATURE [PartDesign::Pad] Pad004
  BaseFeature = -> Fillet
  Direction = (0,0,1)
  Length = 10
  Length2 = 10
  Offset = 7
  Profile = -> Sketch006
  ReferenceAxis = -> Sketch006 [N_Axis]
  Refine = true
  SideType = 0
  Suppressed = false
  Type = 3
  Type2 = 0
  UpToFace = -> Fillet [Face24]
  expr: Offset = Sketch007.Constraints.gap_box_painel
FEATURE [PartDesign::Mirrored] Mirrored002
  MirrorPlane = -> Sketch006 [V_Axis]
  Refine = true
  Suppressed = false
  TransformMode = 0
FEATURE [PartDesign::Mirrored] Mirrored003
  MirrorPlane = -> Sketch006 [H_Axis]
  Refine = true
  Suppressed = false
  TransformMode = 0
FEATURE [PartDesign::MultiTransform] MultiTransform001
  BaseFeature = -> Pad004
  Originals = -> [Pad004]
  Refine = true
  Suppressed = false
  TransformMode = 0
  Transformations = -> [Mirrored002,Mirrored003]
FEATURE [Part::Part2DObjectPython] ShapeString003  # Draft 2D object (typed FeaturePython)
  FontFile = <userpath>/Documents/FreeCAD/Fonts/JetBrainsMonoNerdFont-ExtraBold.ttf
  Fuse = false
  Justification = 4
  JustificationReference = 0
  KeepLeftMargin = false
  MakeFace = true
  ObliqueAngle = 0
  Placement = pos=(3.1e-15,-25,0) rot=(1,0,0;3.14159rad)
  ScaleToSize = true
  Size = 8
  String = Photogate V2
  Tracking = 0
FEATURE [PartDesign::Pocket] Pocket010
  BaseFeature = -> MultiTransform001
  Direction = (0,1e-16,1)
  Length = 0.4
  Length2 = 5
  Profile = -> ShapeString003
  ReferenceAxis = -> ShapeString003 [N_Axis]
  Refine = true
  SideType = 0
  Suppressed = false
  Type = 0
  Type2 = 0
FEATURE [PartDesign::Body] Body001  label="Painel"
  AllowCompound = false
  Group = -> [Sketch001,Pad,Pad001,Sketch002,Pocket,DatumPlane,Sketch003,Pad002,Pocket001,Pocket002,MultiTransform,Mirrored,Mirrored001,Sketch004,Pocket003,Pad003,Sketch005,Pocket004,Fillet,Sketch006,Pad004,MultiTransform001,Mirrored002,Mirrored003,ShapeString003,Pocket010]
  Origin = -> Origin001
  Tip = -> Pocket010
COMPONENT P11 — recipe-attached ("Reforce2Arm001", modeled in this document).
Construction recipe (the document's own serialized feature program — sketch geometry with constraints, then the solid features built on it; lengths are millimeters unless a unit is written):

FEATURE [Sketcher::SketchObject] Sketch046
  ArcFitTolerance = 1e-06
  AttachmentSupport = -> [XY_Plane008]
  ExternalTypes = [0]
  FullyConstrained = true
  MakeInternals = false
  MapMode = 5
  _ExternalGeoVersion = 0
  expr: Constraints[11] = Sketch045.Constraints.reforce_arm_width - 0.2 mm
  sketch-geometry (5):
    g0: LineSegment StartX=-2.89999 StartY=-2.89999 StartZ=0 EndX=2.89999 EndY=-2.89999 EndZ=0
    g1: LineSegment StartX=2.89999 StartY=-2.89999 StartZ=0 EndX=2.89999 EndY=2.89999 EndZ=0
    g2: LineSegment StartX=2.89999 StartY=2.89999 StartZ=0 EndX=-2.89999 EndY=2.89999 EndZ=0
    g3: LineSegment StartX=-2.89999 StartY=2.89999 StartZ=0 EndX=-2.89999 EndY=-2.89999 EndZ=0
    g4: GeomPoint [constr] X=0 Y=0 Z=0
  constraints (12):
    c: Coincident(g0,g1)
    c: Coincident(g1,g2)
    c: Coincident(g2,g3)
    c: Coincident(g3,g0)
    c: Horizontal(g0)
    c: Horizontal(g2)
    c: Vertical(g1)
    c: Vertical(g3)
    c: Symmetric(g2,g0,g4)
    c: Coincident(g4,g-1)
    c: Equal(g0,g1)
    c: DistanceY(g1,g1) = 5.79999
FEATURE [PartDesign::Pad] Pad022
  Direction = (0,0,1)
  Length = 137.1
  Length2 = 10
  Profile = -> Sketch046
  ReferenceAxis = -> Sketch046 [N_Axis]
  Refine = true
  SideType = 0
  Suppressed = false
  Type = 0
  Type2 = 0
  expr: Length = Sketch001.Constraints.display_inner_length + 2 * 6 mm - 0.2 mm
FEATURE [PartDesign::Body] Body007  label="Reforce2Arm"
  AllowCompound = false
  Group = -> [Sketch046,Pad022]
  Origin = -> Origin008
  Tip = -> Pad022
COMPONENT P12 — recipe-attached ("SensorClip001", modeled in this document).
Construction recipe (the document's own serialized feature program — sketch geometry with constraints, then the solid features built on it; lengths are millimeters unless a unit is written):

FEATURE [Sketcher::SketchObject] Sketch060
  ArcFitTolerance = 1e-06
  AttachmentSupport = -> [XY_Plane015]
  ExternalTypes = [0]
  FullyConstrained = false
  MakeInternals = false
  MapMode = 5
  _ExternalGeoVersion = 0
  sketch-geometry (26):
    g0: LineSegment StartX=-2.4 StartY=-10.05 StartZ=0 EndX=7.5 EndY=-10.05 EndZ=0
    g1: LineSegment StartX=7.5 StartY=10.05 StartZ=0 EndX=-2.4 EndY=10.05 EndZ=0
    g2: LineSegment StartX=-7.5 StartY=4.95 StartZ=0 EndX=-7.5 EndY=-4.95 EndZ=0
    g3: GeomPoint [constr] X=0 Y=0 Z=0
    g4: LineSegment StartX=-5.15 StartY=-12.8 StartZ=0 EndX=8.5 EndY=-12.8 EndZ=0
    g5: LineSegment StartX=8.5 StartY=12.8 StartZ=0 EndX=-5.15 EndY=12.8 EndZ=0
    g6: LineSegment StartX=-10.25 StartY=7.7 StartZ=0 EndX=-10.25 EndY=-7.7 EndZ=0
    g7: GeomPoint [constr] X=0 Y=0 Z=0
    g8: ArcOfCircle CenterX=7.5 CenterY=4.95 CenterZ=0 NormalX=0 NormalY=0 NormalZ=1 AngleXU=0 Radius=5.1 StartAngle=-1.8e-15 EndAngle=1.5708
    g9: ArcOfCircle CenterX=7.5 CenterY=-4.95 CenterZ=0 NormalX=0 NormalY=0 NormalZ=1 AngleXU=0 Radius=5.1 StartAngle=4.71239 EndAngle=6.28319
    g10: ArcOfCircle CenterX=-2.4 CenterY=4.95 CenterZ=0 NormalX=0 NormalY=0 NormalZ=1 AngleXU=0 Radius=5.1 StartAngle=1.5708 EndAngle=3.14159
    g11: GeomPoint [constr] X=-7.5 Y=10.05 Z=0
    g12: ArcOfCircle CenterX=-2.4 CenterY=-4.95 CenterZ=0 NormalX=0 NormalY=0 NormalZ=1 AngleXU=0 Radius=5.1 StartAngle=3.14159 EndAngle=4.71239
    g13: GeomPoint [constr] X=-7.5 Y=-10.05 Z=0
    g14: ArcOfCircle CenterX=-5.15 CenterY=7.7 CenterZ=0 NormalX=0 NormalY=0 NormalZ=1 AngleXU=0 Radius=5.1 StartAngle=1.5708 EndAngle=3.14159
    g15: GeomPoint [constr] X=-10.25 Y=12.8 Z=0
    g16: ArcOfCircle CenterX=-5.15 CenterY=-7.7 CenterZ=0 NormalX=0 NormalY=0 NormalZ=1 AngleXU=0 Radius=5.1 StartAngle=3.14159 EndAngle=4.71239
    g17: GeomPoint [constr] X=-10.25 Y=-12.8 Z=0
    g18: ArcOfCircle CenterX=8.5 CenterY=7.7 CenterZ=0 NormalX=0 NormalY=0 NormalZ=1 AngleXU=0 Radius=5.1 StartAngle=0 EndAngle=1.5708
    g19: GeomPoint [constr] X=18.2979 Y=12.8 Z=0
    g20: ArcOfCircle CenterX=8.5 CenterY=-7.7 CenterZ=0 NormalX=0 NormalY=0 NormalZ=1 AngleXU=0 Radius=5.1 StartAngle=4.71239 EndAngle=6.28319
    g21: GeomPoint [constr] X=18.2979 Y=-12.8 Z=0
    g22: LineSegment StartX=13.6 StartY=-7.7 StartZ=0 EndX=13.6 EndY=-4.95 EndZ=0
    g23: LineSegment StartX=13.6 StartY=-4.95 StartZ=0 EndX=12.6 EndY=-4.95 EndZ=0
    g24: LineSegment StartX=12.6 StartY=4.95 StartZ=0 EndX=13.6 EndY=4.95 EndZ=0
    g25: LineSegment StartX=13.6 StartY=7.7 StartZ=0 EndX=13.6 EndY=4.95 EndZ=0
  constraints (58):
    c: Horizontal(g0)
    c: Horizontal(g1)
    c: Vertical(g2)
    c: Symmetric(g1,g13,g3)
    c: Coincident(g3,g-1)
    c: Horizontal(g4)
    c: Horizontal(g5)
    c: Vertical(g6)
    c: Coincident(g7,g3)
    c: Tangent(g8,g1) = -1.5708
    c: Tangent(g9,g0) = -1.5708
    c: Radius(g9) = 5.1
    c: PointOnObject(g11,g1)
    c: PointOnObject(g11,g2)
    c: Tangent(g1,g10) = -1.5708
    c: Tangent(g2,g10) = -1.5708
    c: PointOnObject(g13,g0)
    c: PointOnObject(g13,g2)
    c: Tangent(g0,g12) = -1.5708
    c: Tangent(g2,g12) = -1.5708
    c: Equal(g12,g9)
    c: Equal(g8,g10)
    c: PointOnObject(g15,g5)
    c: PointOnObject(g15,g6)
    c: Tangent(g5,g14) = -1.5708
    c: Tangent(g6,g14) = -1.5708
    c: PointOnObject(g17,g4)
    c: PointOnObject(g17,g6)
    c: Tangent(g4,g16) = -1.5708
    c: Tangent(g6,g16) = -1.5708
    c: Equal(g16,g12)
    c: Equal(g10,g14)
    c: DistanceY(g0,g1) = 20.1
    c: PointOnObject(g19,g5)
    c: Tangent(g5,g18) = -1.5708
    c: PointOnObject(g21,g4)
    c: Tangent(g4,g20) = -1.5708
    c: Equal(g20,g9)
    c: Equal(g18,g8)
    c: Vertical(g22)
    c: Coincident(g23,g22)
    c: Coincident(g23,g9)
    c: Coincident(g24,g8)
    c: Horizontal(g24)
    c: Coincident(g25,g24)
    c: Vertical(g25)
    c: Tangent(g25,g18) = 1.5708
    c: Tangent(g22,g20) = -1.5708
    c: Perpendicular(g9,g23)
    c: Perpendicular(g8,g24)
    c: Horizontal(g23)
    c: DistanceX(g23,g23) = 1
    c: Symmetric(g22,g24,g-1)
    c: Equal(g1,g0)
    c: DistanceX(g2,g8) = 20.1
    c: DistanceY(g1,g5) = 2.75
    c: DistanceY(g4,g0) = 2.75
    c: DistanceX(g6,g2) = 2.75
FEATURE [PartDesign::Pad] Pad035
  Direction = (0,0,1)
  Length = 10
  Length2 = 10
  Profile = -> Sketch060
  ReferenceAxis = -> Sketch060 [N_Axis]
  Refine = true
  SideType = 0
  Suppressed = false
  Type = 0
  Type2 = 0
FEATURE [PartDesign::Fillet] Fillet007
  Base = -> Pad035 [Face20,Face19]
  BaseFeature = -> Pad035
  Radius = 0.5
  Refine = true
  SupportTransform = false
  Suppressed = false
  UseAllEdges = false
FEATURE [PartDesign::Body] Body011  label="SensorClip"
  AllowCompound = false
  Group = -> [Sketch060,Pad035,Fillet007]
  Origin = -> Origin015
  Tip = -> Fillet007
COMPONENT P13 — same part as P12; its construction recipe is shown at P12.
COMPONENT P14 — recipe-attached ("SensorHolder001", modeled in this document).
Construction recipe (the document's own serialized feature program — sketch geometry with constraints, then the solid features built on it; lengths are millimeters unless a unit is written):

FEATURE [Sketcher::SketchObject] Sketch055
  ArcFitTolerance = 1e-06
  AttachmentSupport = -> [XY_Plane011]
  ExternalTypes = [0]
  FullyConstrained = true
  MakeInternals = false
  MapMode = 5
  _ExternalGeoVersion = 0
  sketch-geometry (9):
    g0: ArcOfCircle CenterX=0 CenterY=0 CenterZ=0 NormalX=0 NormalY=0 NormalZ=1 AngleXU=0 Radius=3 StartAngle=0.848062 EndAngle=5.43512
    g1: ArcOfCircle CenterX=0 CenterY=0 CenterZ=0 NormalX=0 NormalY=0 NormalZ=1 AngleXU=0 Radius=5 StartAngle=1.5708 EndAngle=4.71239
    g2: LineSegment StartX=3e-16 StartY=5 StartZ=0 EndX=8 EndY=5 EndZ=0
    g3: LineSegment StartX=8 StartY=5 StartZ=0 EndX=8 EndY=2.25 EndZ=0
    g4: LineSegment StartX=8 StartY=2.25 StartZ=0 EndX=1.98431 EndY=2.25 EndZ=0
    g5: LineSegment StartX=-6.17132e-06 StartY=-5 StartZ=0 EndX=8 EndY=-5 EndZ=0
    g6: LineSegment StartX=8 StartY=-5 StartZ=0 EndX=8 EndY=-2.25 EndZ=0
    g7: LineSegment StartX=8 StartY=-2.25 StartZ=0 EndX=1.98431 EndY=-2.25 EndZ=0
    g8: Circle [constr] CenterX=0 CenterY=0 CenterZ=0 NormalX=0 NormalY=0 NormalZ=1 AngleXU=0 Radius=3
  constraints (25):
    c: Coincident(g0,g-1)
    c: Coincident(g1,g0)
    c: Coincident(g2,g3)
    c: Coincident(g3,g4)
    c: Vertical(g3)
    c: Horizontal(g2)
    c: Horizontal(g4)
    c: Coincident(g5,g6)
    c: Coincident(g6,g7)
    c: Vertical(g6)
    c: Horizontal(g5)
    c: Horizontal(g7)
    c: Diameter(g0) = 6
    c: Vertical(g6,g3)
    c: Vertical(g4,g7)
    c: Distance(g3,g6) = 4.5
    c: DistanceX(g2,g2) = 8
    c: Coincident(g4,g0)
    c: Coincident(g0,g7)
    c: Coincident(g1,g5)
    c: Equal(g6,g3)
    c: Tangent(g2,g1) = 1.5708
    c: Diameter(g1) = 10
    c: Coincident(g8,g0)
    c: PointOnObject(g0,g8)
FEATURE [PartDesign::Pad] Pad031
  Direction = (0,0,1)
  Length = 10
  Length2 = 10
  Profile = -> Sketch055
  ReferenceAxis = -> Sketch055 [N_Axis]
  Refine = true
  SideType = 2
  Suppressed = false
  Type = 0
  Type2 = 0
FEATURE [Sketcher::SketchObject] Sketch056
  ArcFitTolerance = 1e-06
  AttachmentSupport = -> [XZ_Plane011]
  ExternalGeometry = -> [Pad031]
  ExternalTypes = [0]
  FullyConstrained = true
  MakeInternals = false
  MapMode = 5
  Placement = pos=(0,0,0) rot=(1,0,0;1.5708rad)
  _ExternalGeoVersion = 0
  sketch-geometry (2):
    g0: Circle CenterX=4.75 CenterY=0 CenterZ=0 NormalX=0 NormalY=0 NormalZ=1 AngleXU=0 Radius=1.75
    g1: LineSegment [constr] StartX=3 StartY=5 StartZ=0 EndX=3 EndY=-5 EndZ=0
  constraints (6):
    c: Diameter(g0) = 3.5
    c: Coincident(g1,g-3)
    c: Vertical(g1)
    c: Tangent(g0,g1)
    c: Horizontal(g-4,g1)
    c: PointOnObject(g0,g-1)
FEATURE [PartDesign::Pocket] Pocket028
  BaseFeature = -> Pad031
  Direction = (0,1,-2e-16)
  Length = 5
  Length2 = 5
  Profile = -> Sketch056
  ReferenceAxis = -> Sketch056 [N_Axis]
  Refine = true
  SideType = 2
  Suppressed = false
  Type = 1
  Type2 = 0
FEATURE [PartDesign::Body] Body009  label="SensorHolder"
  AllowCompound = false
  Group = -> [Sketch055,Pad031,Sketch056,Pocket028]
  Origin = -> Origin011
  Tip = -> Pocket028
COMPONENT P15 — same part as P14; its construction recipe is shown at P14.
COMPONENT P16 — recipe-attached ("SensorThumbScrew001", modeled in this document).
Construction recipe (the document's own serialized feature program — sketch geometry with constraints, then the solid features built on it; lengths are millimeters unless a unit is written):

FEATURE [Sketcher::SketchObject] Sketch058
  ArcFitTolerance = 1e-06
  AttachmentSupport = -> [XY_Plane013]
  ExternalTypes = [0]
  FullyConstrained = true
  MakeInternals = false
  MapMode = 5
  _ExternalGeoVersion = 0
  sketch-geometry (10):
    g0: Circle CenterX=0 CenterY=0 CenterZ=0 NormalX=0 NormalY=0 NormalZ=1 AngleXU=0 Radius=1.55
    g1: LineSegment StartX=5 StartY=2.07107 StartZ=0 EndX=2.07107 EndY=5 EndZ=0
    g2: LineSegment StartX=2.07107 StartY=5 StartZ=0 EndX=-2.07107 EndY=5 EndZ=0
    g3: LineSegment StartX=-2.07107 StartY=5 StartZ=0 EndX=-5 EndY=2.07107 EndZ=0
    g4: LineSegment StartX=-5 StartY=2.07107 StartZ=0 EndX=-5 EndY=-2.07107 EndZ=0
    g5: LineSegment StartX=-5 StartY=-2.07107 StartZ=0 EndX=-2.07107 EndY=-5 EndZ=0
    g6: LineSegment StartX=-2.07107 StartY=-5 StartZ=0 EndX=2.07107 EndY=-5 EndZ=0
    g7: LineSegment StartX=2.07107 StartY=-5 StartZ=0 EndX=5 EndY=-2.07107 EndZ=0
    g8: LineSegment StartX=5 StartY=-2.07107 StartZ=0 EndX=5 EndY=2.07107 EndZ=0
    g9: Circle [constr] CenterX=0 CenterY=0 CenterZ=0 NormalX=0 NormalY=0 NormalZ=1 AngleXU=0 Radius=5.41196
  constraints (22):
    c: Diameter(g0) = 3.1
    c: Coincident(g1,g2)
    c: Coincident(g2,g3)
    c: Coincident(g3,g4)
    c: Coincident(g4,g5)
    c: Coincident(g5,g6)
    c: Coincident(g6,g7)
    c: Coincident(g7,g8)
    c: Coincident(g8,g1)
    c: Equal(g1, g2-g8) x7
    c: PointOnObject(g1,g9)
    c: PointOnObject(g2,g9)
    c: PointOnObject(g3,g9)
    c: PointOnObject(g4,g9)
    c: PointOnObject(g5,g9)
    c: PointOnObject(g6,g9)
    c: PointOnObject(g7,g9)
    c: PointOnObject(g8,g9)
    c: Coincident(g9,g0)
    c: Vertical(g8)
    c: DistanceY(g6,g1) = 10
    c: Coincident(g0,g-1)
FEATURE [PartDesign::Pad] Pad034
  Direction = (0,0,1)
  Length = 6.5
  Length2 = 10
  Profile = -> Sketch058
  ReferenceAxis = -> Sketch058 [N_Axis]
  Refine = true
  Reversed = true
  SideType = 0
  Suppressed = false
  Type = 0
  Type2 = 0
FEATURE [Sketcher::SketchObject] Sketch059
  ArcFitTolerance = 1e-06
  AttachmentSupport = -> [XY_Plane013]
  ExternalTypes = [0]
  FullyConstrained = true
  MakeInternals = false
  MapMode = 5
  _ExternalGeoVersion = 0
  sketch-geometry (7):
    g0: LineSegment StartX=1.61658 StartY=2.8 StartZ=0 EndX=-1.61658 EndY=2.8 EndZ=0
    g1: LineSegment StartX=-1.61658 StartY=2.8 StartZ=0 EndX=-3.23316 EndY=0 EndZ=0
    g2: LineSegment StartX=-3.23316 StartY=0 StartZ=0 EndX=-1.61658 EndY=-2.8 EndZ=0
    g3: LineSegment StartX=-1.61658 StartY=-2.8 StartZ=0 EndX=1.61658 EndY=-2.8 EndZ=0
    g4: LineSegment StartX=1.61658 StartY=-2.8 StartZ=0 EndX=3.23316 EndY=0 EndZ=0
    g5: LineSegment StartX=3.23316 StartY=0 StartZ=0 EndX=1.61658 EndY=2.8 EndZ=0
    g6: Circle [constr] CenterX=0 CenterY=0 CenterZ=0 NormalX=0 NormalY=0 NormalZ=1 AngleXU=0 Radius=3.23316
  constraints (16):
    c: Coincident(g0,g1)
    c: Coincident(g1,g2)
    c: Coincident(g2,g3)
    c: Coincident(g3,g4)
    c: Coincident(g4,g5)
    c: Coincident(g5,g0)
    c: Equal(g0, g1-g5) x5
    c: PointOnObject(g0,g6)
    c: PointOnObject(g1,g6)
    c: PointOnObject(g2,g6)
    c: PointOnObject(g3,g6)
    c: PointOnObject(g4,g6)
    c: PointOnObject(g5,g6)
    c: Coincident(g6,g-1)
    c: DistanceY(g3,g0) = 5.6
    c: PointOnObject(g4,g-1)
FEATURE [PartDesign::Pocket] Pocket031
  BaseFeature = -> Pad034
  Direction = (0,0,-1)
  Length = 5.5
  Length2 = 5
  Profile = -> Sketch059
  ReferenceAxis = -> Sketch059 [N_Axis]
  Refine = true
  SideType = 0
  Suppressed = false
  Type = 0
  Type2 = 0
FEATURE [PartDesign::Body] Body010  label="SensorThumbScrew"
  AllowCompound = false
  Group = -> [Sketch058,Pad034,Sketch059,Pocket031]
  Origin = -> Origin013
  Tip = -> Pocket031
COMPONENT P17 — same part as P16; its construction recipe is shown at P16.
